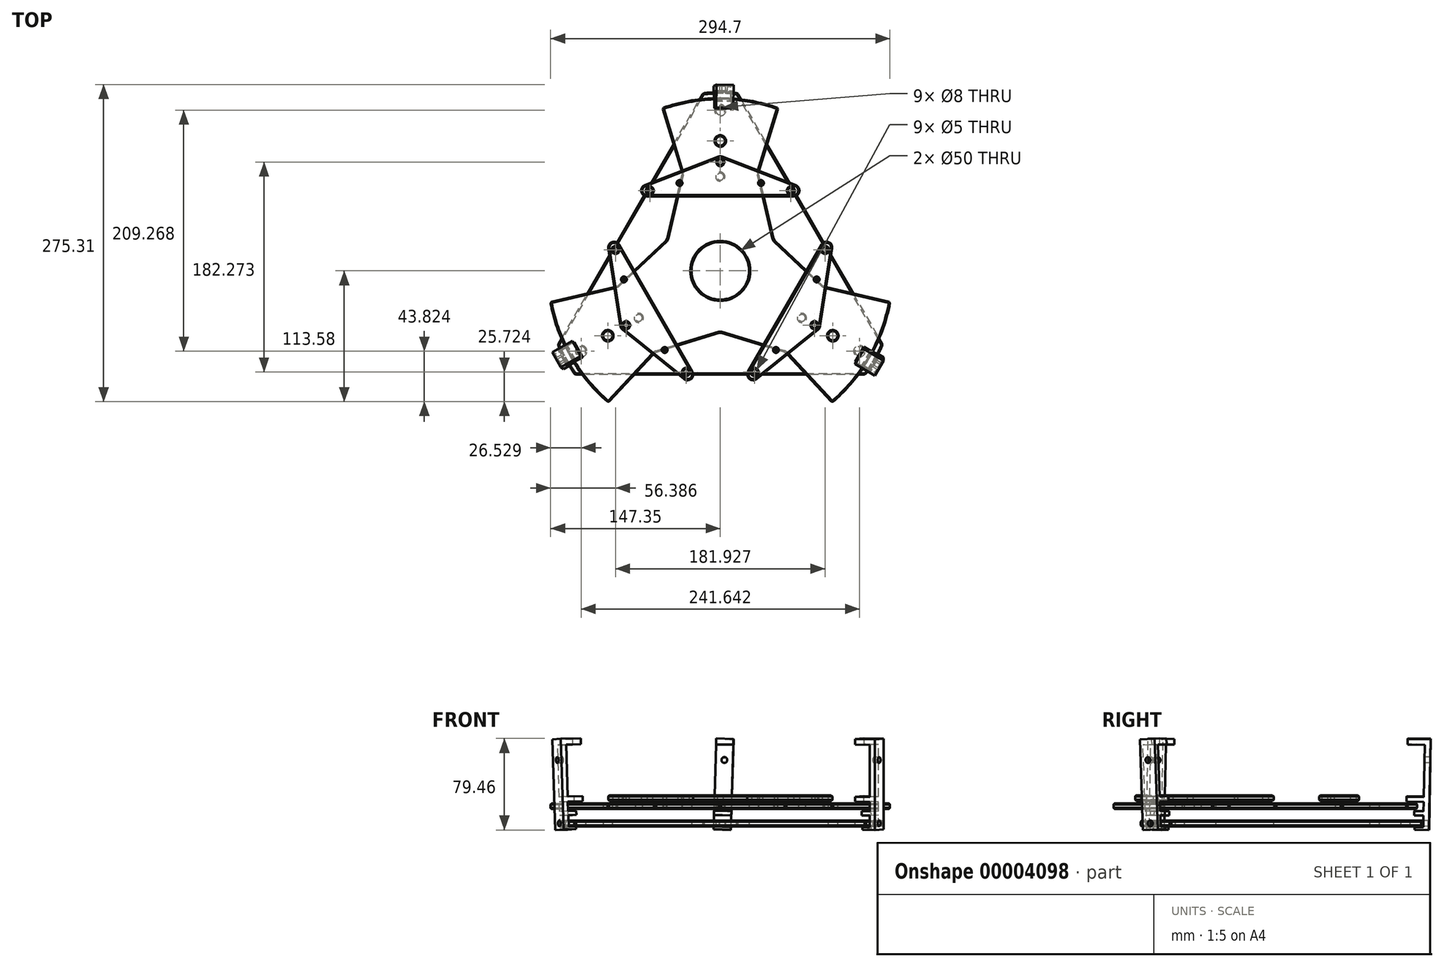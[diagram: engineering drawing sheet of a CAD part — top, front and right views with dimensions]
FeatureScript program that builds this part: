
annotation { "Feature Type Name" : "Feature", "Feature Type Description" : "" }
export const myFeature = defineFeature(function(context is Context, id is Id, definition is map)
    precondition{}
    {
        {
            var Q0;
            Q0=qCreatedBy(makeId("Top.planeOp"),FACE);
            var sketch = newSketch(context, id + "F0", { "sketchPlane" : qUnion([Q0])});
            skArc(sketch, "E0", {"start": v(-141.07, -64.21) * mm, "mid": v(-134.23, -77.5) * mm, "end": v(-126.15, -90.07) * mm});
            skCircle(sketch, "E1.cCircle", {"center": v(0, 0) * mm, "radius": 90.07 * mm, "construction": true});
            skLineSegment(sketch, "E1.0", {"start": v(14.93, 154.28) * mm, "end": v(141.07, -64.21) * mm});
            skLineSegment(sketch, "E1.1", {"start": v(126.15, -90.07) * mm, "end": v(-126.15, -90.07) * mm});
            skLineSegment(sketch, "E1.2", {"start": v(-141.07, -64.21) * mm, "end": v(-14.93, 154.28) * mm});
            skPoint(sketch, "E1.0.midPoint", {"position": v(78, 45.03) * mm});
            skPoint(sketch, "E2.orphan", {"position": v(0, 180.13) * mm});
            skPoint(sketch, "E3.orphan", {"position": v(-156, -90.07) * mm});
            skPoint(sketch, "E4.orphan", {"position": v(156, -90.07) * mm});
            skArc(sketch, "E5.trimOffspring", {"start": v(126.15, -90.07) * mm, "mid": v(134.23, -77.5) * mm, "end": v(141.07, -64.21) * mm});
            skArc(sketch, "E6.trimOffspring", {"start": v(14.93, 154.28) * mm, "mid": v(0, 155) * mm, "end": v(-14.93, 154.28) * mm});
            skCircle(sketch, "E7", {"center": v(0, 0) * mm, "radius": 25 * mm});
            skCircle(sketch, "E8", {"center": v(0, 112.79) * mm, "radius": 4 * mm});
            skCircle(sketch, "E9.1.0", {"center": v(-97.68, -56.4) * mm, "radius": 4 * mm});
            skCircle(sketch, "E9.2.0", {"center": v(97.68, -56.4) * mm, "radius": 4 * mm});
            skCircle(sketch, "E10", {"center": v(0, 139.51) * mm, "radius": 4 * mm});
            skCircle(sketch, "E11.1.0", {"center": v(-120.82, -69.76) * mm, "radius": 4 * mm});
            skCircle(sketch, "E11.2.0", {"center": v(120.82, -69.76) * mm, "radius": 4 * mm});
            skSolve(sketch);
        }
        {
            var Q0;
            Q0=makeQuery(id+"F0.imprint","IMPRINT",FACE,{"disambiguationData":[TD([[makeQuery(id+"F0.imprint","IMPRINT",EDGE,{"derivedFrom":sQuery(id+"F0.wireOp",EDGE,"E0")}),1.0]])]});
            extrude(context, id + "F1", {"entities" : qUnion([Q0]), "depth" : 5 * mm});
        }
        {
            var Q0;
            Q0=makeQuery(id+"F1.opExtrude","CAP_FACE",FACE,{"disambiguationData":[OSD([sQuery(id+"F0.wireOp",EDGE,"E0"),sQuery(id+"F0.wireOp",EDGE,"E1.0"),sQuery(id+"F0.wireOp",EDGE,"E1.1"),sQuery(id+"F0.wireOp",EDGE,"E1.2"),sQuery(id+"F0.wireOp",EDGE,"E5.trimOffspring"),sQuery(id+"F0.wireOp",EDGE,"E6.trimOffspring"),sQuery(id+"F0.wireOp",EDGE,"E7"),sQuery(id+"F0.wireOp",EDGE,"E8"),sQuery(id+"F0.wireOp",EDGE,"E9.1.0"),sQuery(id+"F0.wireOp",EDGE,"E9.2.0"),sQuery(id+"F0.wireOp",EDGE,"E10"),sQuery(id+"F0.wireOp",EDGE,"E11.1.0"),sQuery(id+"F0.wireOp",EDGE,"E11.2.0")])],"isStart":false});
            cPlane(context, id + "F2", {"entities" : qUnion([Q0]), "cplaneType" : CPlaneType.OFFSET, "offset" : 10 * mm, "width" : 150 * mm, "height" : 150 * mm});
        }
        {
            var Q0;
            Q0=qCreatedBy(id+"F2.planeOp",FACE);
            var sketch = newSketch(context, id + "F3", { "sketchPlane" : qUnion([Q0])});
            skCircle(sketch, "E12.0", {"center": v(0, 0) * mm, "radius": 25 * mm});
            skArc(sketch, "E13.0", {"start": v(14.93, 154.28) * mm, "mid": v(0, 155) * mm, "end": v(-14.93, 154.28) * mm, "construction": true});
            skLineSegment(sketch, "E14", {"start": v(-50.32, 141.3) * mm, "end": v(-32.94, 84.6) * mm});
            skCircle(sketch, "E15", {"center": v(0, 0) * mm, "radius": 53.68 * mm, "construction": true});
            skLineSegment(sketch, "E16", {"start": v(-32.94, 84.6) * mm, "end": v(-46.49, 26.84) * mm});
            skCircle(sketch, "E17.cCircle", {"center": v(0, 0) * mm, "radius": 26.84 * mm, "construction": true});
            skLineSegment(sketch, "E17.0", {"start": v(-46.49, 26.84) * mm, "end": v(46.49, 26.84) * mm, "construction": true});
            skLineSegment(sketch, "E17.1", {"start": v(46.49, 26.84) * mm, "end": v(0, -53.68) * mm, "construction": true});
            skLineSegment(sketch, "E17.2", {"start": v(0, -53.68) * mm, "end": v(-46.49, 26.84) * mm, "construction": true});
            skPoint(sketch, "E17.0.midPoint", {"position": v(0, 26.84) * mm});
            skLineSegment(sketch, "E18.0.MirrorCS", {"start": v(32.94, 84.6) * mm, "end": v(46.49, 26.84) * mm});
            skLineSegment(sketch, "E18.1.MirrorCS", {"start": v(50.32, 141.3) * mm, "end": v(32.94, 84.6) * mm});
            skArc(sketch, "E19.0", {"start": v(-50.32, 141.3) * mm, "mid": v(0, 150) * mm, "end": v(50.32, 141.3) * mm});
            skLineSegment(sketch, "E20.1.0", {"start": v(-56.79, -70.82) * mm, "end": v(0, -53.68) * mm});
            skLineSegment(sketch, "E20.1.1", {"start": v(-97.22, -114.23) * mm, "end": v(-56.79, -70.82) * mm});
            skArc(sketch, "E20.1.2", {"start": v(-97.22, -114.23) * mm, "mid": v(-129.9, -75) * mm, "end": v(-147.54, -27.08) * mm});
            skLineSegment(sketch, "E20.1.3", {"start": v(-147.54, -27.08) * mm, "end": v(-89.73, -13.77) * mm});
            skLineSegment(sketch, "E20.1.4", {"start": v(-89.73, -13.77) * mm, "end": v(-46.49, 26.84) * mm});
            skLineSegment(sketch, "E20.2.0", {"start": v(89.73, -13.77) * mm, "end": v(46.49, 26.84) * mm});
            skLineSegment(sketch, "E20.2.1", {"start": v(147.54, -27.08) * mm, "end": v(89.73, -13.77) * mm});
            skArc(sketch, "E20.2.2", {"start": v(147.54, -27.08) * mm, "mid": v(129.9, -75) * mm, "end": v(97.22, -114.23) * mm});
            skLineSegment(sketch, "E20.2.3", {"start": v(97.22, -114.23) * mm, "end": v(56.79, -70.82) * mm});
            skLineSegment(sketch, "E20.2.4", {"start": v(56.79, -70.82) * mm, "end": v(0, -53.68) * mm});
            skCircle(sketch, "E21.0", {"center": v(-97.68, -56.4) * mm, "radius": 4 * mm});
            skCircle(sketch, "E22.0", {"center": v(0, 112.79) * mm, "radius": 4 * mm});
            skCircle(sketch, "E23.0", {"center": v(97.68, -56.4) * mm, "radius": 4 * mm});
            skCircle(sketch, "E24", {"center": v(0, 81.76) * mm, "radius": 3 * mm});
            skCircle(sketch, "E25.1.0", {"center": v(-70.8, -40.88) * mm, "radius": 3 * mm});
            skCircle(sketch, "E25.2.0", {"center": v(70.8, -40.88) * mm, "radius": 3 * mm});
            skSolve(sketch);
        }
        {
            var Q0;
            Q0=makeQuery(id+"F3.imprint","IMPRINT",FACE,{"disambiguationData":[TD([[makeQuery(id+"F3.imprint","IMPRINT",EDGE,{"derivedFrom":sQuery(id+"F3.wireOp",EDGE,"E12.0")}),-1.0]])]});
            extrude(context, id + "F4", {"entities" : qUnion([Q0]), "depth" : 5 * mm});
        }
        {
            var Q0;
            Q0=makeQuery(id+"F4.opExtrude","CAP_FACE",FACE,{"disambiguationData":[OSD([sQuery(id+"F3.wireOp",EDGE,"E12.0"),sQuery(id+"F3.wireOp",EDGE,"E14"),sQuery(id+"F3.wireOp",EDGE,"E16"),sQuery(id+"F3.wireOp",EDGE,"E18.0.MirrorCS"),sQuery(id+"F3.wireOp",EDGE,"E18.1.MirrorCS"),sQuery(id+"F3.wireOp",EDGE,"E19.0"),sQuery(id+"F3.wireOp",EDGE,"E20.1.0"),sQuery(id+"F3.wireOp",EDGE,"E20.1.1"),sQuery(id+"F3.wireOp",EDGE,"E20.1.2"),sQuery(id+"F3.wireOp",EDGE,"E20.1.3"),sQuery(id+"F3.wireOp",EDGE,"E20.1.4"),sQuery(id+"F3.wireOp",EDGE,"E20.2.0"),sQuery(id+"F3.wireOp",EDGE,"E20.2.1"),sQuery(id+"F3.wireOp",EDGE,"E20.2.2"),sQuery(id+"F3.wireOp",EDGE,"E20.2.3"),sQuery(id+"F3.wireOp",EDGE,"E20.2.4"),sQuery(id+"F3.wireOp",EDGE,"E21.0"),sQuery(id+"F3.wireOp",EDGE,"E22.0"),sQuery(id+"F3.wireOp",EDGE,"E23.0"),sQuery(id+"F3.wireOp",EDGE,"E24"),sQuery(id+"F3.wireOp",EDGE,"E25.1.0"),sQuery(id+"F3.wireOp",EDGE,"E25.2.0")])],"isStart":false});
            cPlane(context, id + "F5", {"entities" : qUnion([Q0]), "cplaneType" : CPlaneType.OFFSET, "offset" : 2 * mm, "width" : 150 * mm, "height" : 150 * mm});
        }
        {
            var Q0;
            Q0=qCreatedBy(id+"F5.planeOp",FACE);
            var sketch = newSketch(context, id + "F6", { "sketchPlane" : qUnion([Q0])});
            skCircle(sketch, "E26", {"center": v(0, 0) * mm, "radius": 94.42 * mm, "construction": true});
            skLineSegment(sketch, "E27", {"start": v(-63.7, 69.7) * mm, "end": v(63.7, 69.7) * mm, "construction": true});
            skLineSegment(sketch, "E28", {"start": v(63.7, 69.7) * mm, "end": v(0, 94.42) * mm, "construction": true});
            skLineSegment(sketch, "E29", {"start": v(0, 94.42) * mm, "end": v(-63.7, 69.7) * mm, "construction": true});
            skLineSegment(sketch, "E30.0", {"start": v(-1.8, 99.08) * mm, "end": v(-65.5, 74.36) * mm});
            skLineSegment(sketch, "E30.1", {"start": v(65.5, 74.36) * mm, "end": v(1.8, 99.08) * mm});
            skLineSegment(sketch, "E30.2", {"start": v(-63.7, 64.7) * mm, "end": v(63.7, 64.7) * mm});
            skLineSegment(sketch, "E31.0", {"start": v(0, 99.78) * mm, "end": v(-90.4, 64.7) * mm, "construction": true});
            skLineSegment(sketch, "E31.1", {"start": v(90.4, 64.7) * mm, "end": v(0, 99.78) * mm, "construction": true});
            skLineSegment(sketch, "E31.2", {"start": v(-90.4, 64.7) * mm, "end": v(90.4, 64.7) * mm, "construction": true});
            skPoint(sketch, "E32.visualSharp", {"position": v(-90.4, 64.7) * mm});
            skArc(sketch, "E32.filletArc", {"start": v(-65.5, 74.36) * mm, "mid": v(-68.6, 68.78) * mm, "end": v(-63.7, 64.7) * mm});
            skPoint(sketch, "E33.visualSharp", {"position": v(90.4, 64.7) * mm});
            skArc(sketch, "E33.filletArc", {"start": v(63.7, 64.7) * mm, "mid": v(68.6, 68.78) * mm, "end": v(65.5, 74.36) * mm});
            skPoint(sketch, "E34.visualSharp", {"position": v(0, 99.78) * mm});
            skArc(sketch, "E34.filletArc", {"start": v(1.8, 99.08) * mm, "mid": v(0, 99.42) * mm, "end": v(-1.8, 99.08) * mm});
            skCircle(sketch, "E35", {"center": v(-35.37, 76.2) * mm, "radius": 1.5 * mm});
            skCircle(sketch, "E36.0.MirrorC", {"center": v(35.37, 76.2) * mm, "radius": 1.5 * mm});
            skCircle(sketch, "E37", {"center": v(0, 94.42) * mm, "radius": 2.5 * mm});
            skCircle(sketch, "E38", {"center": v(-61.2, 69.7) * mm, "radius": 2.5 * mm});
            skCircle(sketch, "E39.0.MirrorC", {"center": v(61.2, 69.7) * mm, "radius": 2.5 * mm});
            skLineSegment(sketch, "E40.1.0", {"start": v(-28.51, -90) * mm, "end": v(-92.2, 20.31) * mm, "construction": true});
            skLineSegment(sketch, "E40.1.1", {"start": v(-84.9, -51.1) * mm, "end": v(-31.65, -93.9) * mm});
            skLineSegment(sketch, "E40.1.2", {"start": v(-81.77, -47.2) * mm, "end": v(-28.51, -90) * mm, "construction": true});
            skPoint(sketch, "E40.1.3", {"position": v(-10.83, -110.63) * mm});
            skLineSegment(sketch, "E40.1.4", {"start": v(-92.2, 20.31) * mm, "end": v(-81.77, -47.2) * mm, "construction": true});
            skArc(sketch, "E40.1.5", {"start": v(-87.88, 22.81) * mm, "mid": v(-93.87, 25.03) * mm, "end": v(-97.15, 19.55) * mm});
            skLineSegment(sketch, "E40.1.6", {"start": v(-97.15, 19.55) * mm, "end": v(-86.7, -47.97) * mm});
            skCircle(sketch, "E40.1.7", {"center": v(-81.77, -47.2) * mm, "radius": 2.5 * mm});
            skCircle(sketch, "E40.1.8", {"center": v(-83.67, -7.47) * mm, "radius": 1.5 * mm});
            skLineSegment(sketch, "E40.1.9", {"start": v(-86.41, -49.9) * mm, "end": v(-10.83, -110.63) * mm, "construction": true});
            skArc(sketch, "E40.1.10", {"start": v(-31.65, -93.9) * mm, "mid": v(-25.26, -93.8) * mm, "end": v(-24.18, -87.5) * mm});
            skCircle(sketch, "E40.1.11", {"center": v(-90.96, 18.16) * mm, "radius": 2.5 * mm});
            skLineSegment(sketch, "E40.1.12", {"start": v(-24.18, -87.5) * mm, "end": v(-87.88, 22.81) * mm});
            skPoint(sketch, "E40.1.13", {"position": v(-86.41, -49.9) * mm});
            skCircle(sketch, "E40.1.14", {"center": v(-48.3, -68.72) * mm, "radius": 1.5 * mm});
            skCircle(sketch, "E40.1.15", {"center": v(-29.76, -87.86) * mm, "radius": 2.5 * mm});
            skArc(sketch, "E40.1.16", {"start": v(-86.7, -47.97) * mm, "mid": v(-86.1, -49.7) * mm, "end": v(-84.9, -51.1) * mm});
            skLineSegment(sketch, "E40.2.0", {"start": v(92.2, 20.31) * mm, "end": v(28.51, -90) * mm, "construction": true});
            skLineSegment(sketch, "E40.2.1", {"start": v(86.7, -47.97) * mm, "end": v(97.15, 19.55) * mm});
            skLineSegment(sketch, "E40.2.2", {"start": v(81.77, -47.2) * mm, "end": v(92.2, 20.31) * mm, "construction": true});
            skPoint(sketch, "E40.2.3", {"position": v(101.23, 45.94) * mm});
            skLineSegment(sketch, "E40.2.4", {"start": v(28.51, -90) * mm, "end": v(81.77, -47.2) * mm, "construction": true});
            skArc(sketch, "E40.2.5", {"start": v(24.18, -87.5) * mm, "mid": v(25.26, -93.8) * mm, "end": v(31.65, -93.9) * mm});
            skLineSegment(sketch, "E40.2.6", {"start": v(31.65, -93.9) * mm, "end": v(84.9, -51.1) * mm});
            skCircle(sketch, "E40.2.7", {"center": v(81.77, -47.2) * mm, "radius": 2.5 * mm});
            skCircle(sketch, "E40.2.8", {"center": v(48.3, -68.72) * mm, "radius": 1.5 * mm});
            skLineSegment(sketch, "E40.2.9", {"start": v(86.41, -49.9) * mm, "end": v(101.23, 45.94) * mm, "construction": true});
            skArc(sketch, "E40.2.10", {"start": v(97.15, 19.55) * mm, "mid": v(93.87, 25.03) * mm, "end": v(87.88, 22.81) * mm});
            skCircle(sketch, "E40.2.11", {"center": v(29.76, -87.86) * mm, "radius": 2.5 * mm});
            skLineSegment(sketch, "E40.2.12", {"start": v(87.88, 22.81) * mm, "end": v(24.18, -87.5) * mm});
            skPoint(sketch, "E40.2.13", {"position": v(86.41, -49.9) * mm});
            skCircle(sketch, "E40.2.14", {"center": v(83.67, -7.47) * mm, "radius": 1.5 * mm});
            skCircle(sketch, "E40.2.15", {"center": v(90.96, 18.16) * mm, "radius": 2.5 * mm});
            skArc(sketch, "E40.2.16", {"start": v(84.9, -51.1) * mm, "mid": v(86.1, -49.7) * mm, "end": v(86.7, -47.97) * mm});
            skSolve(sketch);
        }
        {
            var Q0;
            {Q0=qUnion([makeQuery(id+"F6.imprint","IMPRINT",FACE,{"disambiguationData":[TD([[makeQuery(id+"F6.imprint","IMPRINT",EDGE,{"derivedFrom":sQuery(id+"F6.wireOp",EDGE,"E30.0")}),1.0]])]}),makeQuery(id+"F6.imprint","IMPRINT",FACE,{"disambiguationData":[TD([[makeQuery(id+"F6.imprint","IMPRINT",EDGE,{"derivedFrom":sQuery(id+"F6.wireOp",EDGE,"E40.1.1")}),1.0]])]}),makeQuery(id+"F6.imprint","IMPRINT",FACE,{"disambiguationData":[TD([[makeQuery(id+"F6.imprint","IMPRINT",EDGE,{"derivedFrom":sQuery(id+"F6.wireOp",EDGE,"E40.2.1")}),1.0]])]})]);}
            extrude(context, id + "F7", {"entities" : qUnion([Q0]), "depth" : 5 * mm});
        }
        {
            var Q0;
            Q0=qCreatedBy(makeId("Origin.pointOp"),VERTEX);
            var Q1;
            Q1=makeQuery(id+"F7.opExtrude","CAP_VERTEX",VERTEX,{"disambiguationData":[OSD([sQuery(id+"F6.wireOp",EDGE,"E40.2.6"),sQuery(id+"F6.wireOp",EDGE,"E40.2.16")])],"isStart":true});
            var Q2;
            Q2=makeQuery(id+"F4.opExtrude","CAP_VERTEX",VERTEX,{"disambiguationData":[OSD([sQuery(id+"F3.wireOp",EDGE,"E16"),sQuery(id+"F3.wireOp",EDGE,"E20.1.4")])],"isStart":false});
            cPlane(context, id + "F8", {"entities" : qUnion([Q0, Q1, Q2]), "cplaneType" : CPlaneType.THREE_POINT, "offset" : 150 * mm, "width" : 150 * mm, "height" : 150 * mm});
        }
        {
            var Q0;
            Q0=qCreatedBy(id+"F8.planeOp",FACE);
            var sketch = newSketch(context, id + "F9", { "sketchPlane" : qUnion([Q0])});
            skLineSegment(sketch, "E41.bottom", {"start": v(-155.27, 0) * mm, "end": v(-160.27, 0) * mm});
            skLineSegment(sketch, "E41.left", {"start": v(-155.27, 2.3) * mm, "end": v(-155.27, 12.37) * mm});
            skLineSegment(sketch, "E41.right", {"start": v(-160.27, 0) * mm, "end": v(-160.27, 73.75) * mm});
            skLineSegment(sketch, "E42.0", {"start": v(65.82, -0.5) * mm, "end": v(-154, 7.29) * mm, "construction": true});
            skLineSegment(sketch, "E43.right", {"start": v(-155.27, 20.95) * mm, "end": v(-155.27, 24.23) * mm});
            skPoint(sketch, "E44.0", {"position": v(-140.46, 15.96) * mm});
            skLineSegment(sketch, "E45.top", {"start": v(-147.28, 12.37) * mm, "end": v(-155.27, 12.37) * mm});
            skLineSegment(sketch, "E45.left", {"start": v(-147.24, 16.1) * mm, "end": v(-147.28, 12.37) * mm});
            skLineSegment(sketch, "E46.bottom", {"start": v(-155.27, 73.75) * mm, "end": v(-140.4, 73.75) * mm});
            skLineSegment(sketch, "E46.top", {"start": v(-155.27, 78.7) * mm, "end": v(-140.4, 78.7) * mm});
            skLineSegment(sketch, "E46.right", {"start": v(-140.4, 78.7) * mm, "end": v(-140.4, 73.75) * mm});
            skPoint(sketch, "E47.0", {"position": v(-154.08, 2.3) * mm});
            skLineSegment(sketch, "E48.bottom", {"start": v(-155.27, 0) * mm, "end": v(-147.91, 0) * mm});
            skLineSegment(sketch, "E48.top", {"start": v(-155.27, 2.3) * mm, "end": v(-147.91, 2.3) * mm});
            skLineSegment(sketch, "E48.right", {"start": v(-147.91, 0) * mm, "end": v(-147.91, 2.3) * mm});
            skLineSegment(sketch, "E49.top", {"start": v(-155.27, 78.7) * mm, "end": v(-160.27, 78.7) * mm});
            skLineSegment(sketch, "E49.right", {"start": v(-160.27, 73.75) * mm, "end": v(-160.27, 78.7) * mm});
            skLineSegment(sketch, "E50.bottom", {"start": v(-140.46, 24.23) * mm, "end": v(-155.27, 24.23) * mm});
            skLineSegment(sketch, "E50.top", {"start": v(-140.46, 28.52) * mm, "end": v(-155.27, 28.52) * mm});
            skLineSegment(sketch, "E50.left", {"start": v(-140.46, 24.23) * mm, "end": v(-140.46, 28.52) * mm});
            skLineSegment(sketch, "E51.trimOffspring", {"start": v(-155.27, 28.52) * mm, "end": v(-155.27, 73.75) * mm});
            skLineSegment(sketch, "E52.trimOffspring", {"start": v(-155.27, 15.96) * mm, "end": v(-155.27, 24.23) * mm});
            skLineSegment(sketch, "E53", {"start": v(-147.24, 16.1) * mm, "end": v(-155.27, 15.96) * mm});
            skSolve(sketch);
        }
        {
            var Q0;
            Q0 = qSketchRegion(id + "F9", true);
            extrude(context, id + "F10", {"entities" : qUnion([Q0]), "operationType" : NewBodyOperationType.ADD, "depth" : 15 * mm, "symmetric" : true});
        }
        {
            var Q0;
            Q0=makeQuery(id+"F10.opExtrude","SWEPT_BODY",BODY,{"disambiguationData":[OSD([sQuery(id+"F9.wireOp",EDGE,"E41.bottom"),sQuery(id+"F9.wireOp",EDGE,"E41.left"),sQuery(id+"F9.wireOp",EDGE,"E45.top"),sQuery(id+"F9.wireOp",EDGE,"E45.left"),sQuery(id+"F9.wireOp",EDGE,"E46.bottom"),sQuery(id+"F9.wireOp",EDGE,"E46.top"),sQuery(id+"F9.wireOp",EDGE,"E46.right"),sQuery(id+"F9.wireOp",EDGE,"E48.top"),sQuery(id+"F9.wireOp",EDGE,"E48.right"),sQuery(id+"F9.wireOp",EDGE,"E49.right"),sQuery(id+"F9.wireOp",EDGE,"E50.bottom"),sQuery(id+"F9.wireOp",EDGE,"E50.top"),sQuery(id+"F9.wireOp",EDGE,"E50.left"),sQuery(id+"F9.wireOp",EDGE,"E51.trimOffspring"),sQuery(id+"F9.wireOp",EDGE,"E52.trimOffspring"),sQuery(id+"F9.wireOp",EDGE,"E53")])]});
            var Q1;
            Q1=makeQuery(id+"F4.opExtrude","CAP_EDGE",EDGE,{"disambiguationData":[OSD([sQuery(id+"F3.wireOp",EDGE,"E12.0")])],"isStart":false});
            circularPattern(context, id + "F11", {"entities" : qUnion([Q0]), "axis" : qUnion([Q1]), "angle" : 120 * degree, "instanceCount" : 3, "computeTransformsWithoutBuiltin" : true});
        }
        {
            var Q0;
            Q0=makeQuery(id+"F10.opExtrude","SWEPT_EDGE",EDGE,{"disambiguationData":[OSD([sQuery(id+"F9.wireOp",EDGE,"E46.top"),sQuery(id+"F9.wireOp",EDGE,"E46.right")])]});
            var Q1;
            {var subQ0=sQuery(id+"F9.wireOp",EDGE,"E49.right");Q1=qUnion([makeQuery(id+"F10.opExtrude","SWEPT_EDGE",EDGE,{"disambiguationData":[OSD([sQuery(id+"F9.wireOp",EDGE,"E41.bottom"),subQ0])]}),makeQuery(id+"F10.opExtrude","SWEPT_EDGE",EDGE,{"disambiguationData":[OSD([sQuery(id+"F9.wireOp",EDGE,"E46.top"),subQ0])]})]);}
            var Q2;
            {var subQ0=sQuery(id+"F9.wireOp",EDGE,"E41.bottom");Q2=qUnion([makeQuery(id+"F10.opExtrude","SWEPT_EDGE",EDGE,{"disambiguationData":[OSD([subQ0,sQuery(id+"F9.wireOp",EDGE,"E49.right")])]}),makeQuery(id+"F10.opExtrude","SWEPT_EDGE",EDGE,{"disambiguationData":[OSD([subQ0,sQuery(id+"F9.wireOp",EDGE,"E48.right")])]})]);}
            var Q3;
            Q3=makeQuery(id+"F10.opExtrude","SWEPT_EDGE",EDGE,{"disambiguationData":[OSD([sQuery(id+"F9.wireOp",EDGE,"E50.top"),sQuery(id+"F9.wireOp",EDGE,"E50.left")])]});
            var Q4;
            {var subQ0=sQuery(id+"F9.wireOp",EDGE,"E49.right");Q4=qUnion([makeQuery(id+"F11.opPattern","COPY",EDGE,{"derivedFrom":makeQuery(id+"F10.opExtrude","SWEPT_EDGE",EDGE,{"disambiguationData":[OSD([sQuery(id+"F9.wireOp",EDGE,"E41.bottom"),subQ0])]}),"instanceName":"1"}),makeQuery(id+"F11.opPattern","COPY",EDGE,{"derivedFrom":makeQuery(id+"F10.opExtrude","SWEPT_EDGE",EDGE,{"disambiguationData":[OSD([sQuery(id+"F9.wireOp",EDGE,"E46.top"),subQ0])]}),"instanceName":"1"})]);}
            var Q5;
            Q5=makeQuery(id+"F11.opPattern","COPY",EDGE,{"derivedFrom":makeQuery(id+"F10.opExtrude","CAP_EDGE",EDGE,{"disambiguationData":[OSD([sQuery(id+"F9.wireOp",EDGE,"E41.left")])],"isStart":false}),"instanceName":"1"});
            var Q6;
            Q6=makeQuery(id+"F7.opExtrude","CAP_EDGE",EDGE,{"disambiguationData":[OSD([sQuery(id+"F6.wireOp",EDGE,"E40.1.1")])],"isStart":true});
            var Q7;
            Q7=makeQuery(id+"F11.opPattern","COPY",EDGE,{"derivedFrom":makeQuery(id+"F10.opExtrude","CAP_EDGE",EDGE,{"disambiguationData":[OSD([sQuery(id+"F9.wireOp",EDGE,"E41.left")])],"isStart":false}),"instanceName":"2"});
            var Q8;
            Q8=makeQuery(id+"F4.opExtrude","CAP_EDGE",EDGE,{"disambiguationData":[OSD([sQuery(id+"F3.wireOp",EDGE,"E23.0")])],"isStart":false});
            var Q9;
            Q9=makeQuery(id+"F11.opPattern","COPY",EDGE,{"derivedFrom":makeQuery(id+"F10.opExtrude","SWEPT_EDGE",EDGE,{"disambiguationData":[OSD([sQuery(id+"F9.wireOp",EDGE,"E50.top"),sQuery(id+"F9.wireOp",EDGE,"E50.left")])]}),"instanceName":"1"});
            var Q10;
            {var subQ0=sQuery(id+"F9.wireOp",EDGE,"E41.left");var subQ1=sQuery(id+"F9.wireOp",EDGE,"E50.top");Q10=qUnion([makeQuery(id+"F11.opPattern","COPY",EDGE,{"derivedFrom":makeQuery(id+"F10.opExtrude","SWEPT_EDGE",EDGE,{"disambiguationData":[OSD([subQ0,sQuery(id+"F9.wireOp",EDGE,"E48.top")])]}),"instanceName":"1"}),makeQuery(id+"F11.opPattern","COPY",EDGE,{"derivedFrom":makeQuery(id+"F10.opExtrude","SWEPT_EDGE",EDGE,{"disambiguationData":[OSD([subQ0,sQuery(id+"F9.wireOp",EDGE,"E45.top")])]}),"instanceName":"1"}),makeQuery(id+"F11.opPattern","COPY",EDGE,{"derivedFrom":makeQuery(id+"F10.opExtrude","SWEPT_EDGE",EDGE,{"disambiguationData":[OSD([subQ1,sQuery(id+"F9.wireOp",EDGE,"E50.left")])]}),"instanceName":"1"}),makeQuery(id+"F11.opPattern","COPY",EDGE,{"derivedFrom":makeQuery(id+"F10.opExtrude","SWEPT_EDGE",EDGE,{"disambiguationData":[OSD([subQ1,sQuery(id+"F9.wireOp",EDGE,"E51.trimOffspring")])]}),"instanceName":"1"})]);}
            var Q11;
            Q11=makeQuery(id+"F7.opExtrude","CAP_EDGE",EDGE,{"disambiguationData":[OSD([sQuery(id+"F6.wireOp",EDGE,"E40.1.1")])],"isStart":false});
            var Q12;
            Q12=makeQuery(id+"F7.opExtrude","CAP_EDGE",EDGE,{"disambiguationData":[OSD([sQuery(id+"F6.wireOp",EDGE,"E32.filletArc")])],"isStart":false});
            var Q13;
            Q13=makeQuery(id+"F11.opPattern","COPY",EDGE,{"derivedFrom":makeQuery(id+"F10.opExtrude","SWEPT_EDGE",EDGE,{"disambiguationData":[OSD([sQuery(id+"F9.wireOp",EDGE,"E50.bottom"),sQuery(id+"F9.wireOp",EDGE,"E50.left")])]}),"instanceName":"1"});
            var Q14;
            Q14=makeQuery(id+"F11.opPattern","COPY",EDGE,{"derivedFrom":makeQuery(id+"F10.opExtrude","SWEPT_EDGE",EDGE,{"disambiguationData":[OSD([sQuery(id+"F9.wireOp",EDGE,"E46.bottom"),sQuery(id+"F9.wireOp",EDGE,"E46.right")])]}),"instanceName":"1"});
            var Q15;
            Q15=makeQuery(id+"F11.opPattern","COPY",EDGE,{"derivedFrom":makeQuery(id+"F10.opExtrude","SWEPT_EDGE",EDGE,{"disambiguationData":[OSD([sQuery(id+"F9.wireOp",EDGE,"E46.top"),sQuery(id+"F9.wireOp",EDGE,"E46.right")])]}),"instanceName":"1"});
            var Q16;
            Q16=makeQuery(id+"F7.opExtrude","CAP_EDGE",EDGE,{"disambiguationData":[OSD([sQuery(id+"F6.wireOp",EDGE,"E30.2")])],"isStart":false});
            var Q17;
            Q17=makeQuery(id+"F7.opExtrude","CAP_EDGE",EDGE,{"disambiguationData":[OSD([sQuery(id+"F6.wireOp",EDGE,"E40.1.12")])],"isStart":false});
            var Q18;
            Q18=makeQuery(id+"F4.opExtrude","CAP_EDGE",EDGE,{"disambiguationData":[OSD([sQuery(id+"F3.wireOp",EDGE,"E20.2.1")])],"isStart":false});
            var Q19;
            Q19=makeQuery(id+"F4.opExtrude","CAP_EDGE",EDGE,{"disambiguationData":[OSD([sQuery(id+"F3.wireOp",EDGE,"E18.1.MirrorCS")])],"isStart":false});
            var Q20;
            Q20=makeQuery(id+"F11.opPattern","COPY",EDGE,{"derivedFrom":makeQuery(id+"F10.opExtrude","SWEPT_EDGE",EDGE,{"disambiguationData":[OSD([sQuery(id+"F9.wireOp",EDGE,"E46.top"),sQuery(id+"F9.wireOp",EDGE,"E46.right")])]}),"instanceName":"2"});
            var Q21;
            Q21=makeQuery(id+"F11.opPattern","COPY",EDGE,{"derivedFrom":makeQuery(id+"F10.opExtrude","CAP_EDGE",EDGE,{"disambiguationData":[OSD([sQuery(id+"F9.wireOp",EDGE,"E49.right")])],"isStart":false}),"instanceName":"2"});
            var Q22;
            Q22=makeQuery(id+"F4.opExtrude","CAP_EDGE",EDGE,{"disambiguationData":[OSD([sQuery(id+"F3.wireOp",EDGE,"E20.1.3")])],"isStart":false});
            var Q23;
            Q23=makeQuery(id+"F4.opExtrude","CAP_EDGE",EDGE,{"disambiguationData":[OSD([sQuery(id+"F3.wireOp",EDGE,"E14")])],"isStart":false});
            var Q24;
            Q24=makeQuery(id+"F4.opExtrude","CAP_EDGE",EDGE,{"disambiguationData":[OSD([sQuery(id+"F3.wireOp",EDGE,"E18.1.MirrorCS")])],"isStart":true});
            var Q25;
            Q25=makeQuery(id+"F10.opExtrude","CAP_EDGE",EDGE,{"disambiguationData":[OSD([sQuery(id+"F9.wireOp",EDGE,"E50.bottom")])],"isStart":true});
            var Q26;
            Q26=makeQuery(id+"F4.opExtrude","CAP_EDGE",EDGE,{"disambiguationData":[OSD([sQuery(id+"F3.wireOp",EDGE,"E19.0")])],"isStart":false});
            var Q27;
            Q27=makeQuery(id+"F4.opExtrude","CAP_EDGE",EDGE,{"disambiguationData":[OSD([sQuery(id+"F3.wireOp",EDGE,"E20.2.2")])],"isStart":false});
            var Q28;
            Q28=makeQuery(id+"F11.opPattern","COPY",EDGE,{"derivedFrom":makeQuery(id+"F10.opExtrude","CAP_EDGE",EDGE,{"disambiguationData":[OSD([sQuery(id+"F9.wireOp",EDGE,"E46.top")])],"isStart":false}),"instanceName":"1"});
            var Q29;
            Q29=makeQuery(id+"F11.opPattern","COPY",EDGE,{"derivedFrom":makeQuery(id+"F10.opExtrude","CAP_EDGE",EDGE,{"disambiguationData":[OSD([sQuery(id+"F9.wireOp",EDGE,"E46.top")])],"isStart":false}),"instanceName":"2"});
            var Q30;
            Q30=makeQuery(id+"F7.opExtrude","CAP_EDGE",EDGE,{"disambiguationData":[OSD([sQuery(id+"F6.wireOp",EDGE,"E40.1.6")])],"isStart":false});
            var Q31;
            Q31=makeQuery(id+"F7.opExtrude","CAP_EDGE",EDGE,{"disambiguationData":[OSD([sQuery(id+"F6.wireOp",EDGE,"E40.2.12")])],"isStart":false});
            var Q32;
            Q32=makeQuery(id+"F10.opExtrude","CAP_EDGE",EDGE,{"disambiguationData":[OSD([sQuery(id+"F9.wireOp",EDGE,"E46.bottom")])],"isStart":true});
            var Q33;
            Q33=makeQuery(id+"F10.opExtrude","CAP_EDGE",EDGE,{"disambiguationData":[OSD([sQuery(id+"F9.wireOp",EDGE,"E49.right")])],"isStart":false});
            var Q34;
            Q34=makeQuery(id+"F4.opExtrude","CAP_EDGE",EDGE,{"disambiguationData":[OSD([sQuery(id+"F3.wireOp",EDGE,"E20.2.2")])],"isStart":true});
            var Q35;
            Q35=makeQuery(id+"F4.opExtrude","CAP_EDGE",EDGE,{"disambiguationData":[OSD([sQuery(id+"F3.wireOp",EDGE,"E20.1.2")])],"isStart":false});
            var Q36;
            Q36=makeQuery(id+"F7.opExtrude","CAP_EDGE",EDGE,{"disambiguationData":[OSD([sQuery(id+"F6.wireOp",EDGE,"E40.2.1")])],"isStart":true});
            var Q37;
            Q37=makeQuery(id+"F10.opExtrude","CAP_EDGE",EDGE,{"disambiguationData":[OSD([sQuery(id+"F9.wireOp",EDGE,"E50.top")])],"isStart":true});
            var Q38;
            Q38=makeQuery(id+"F10.opExtrude","CAP_EDGE",EDGE,{"disambiguationData":[OSD([sQuery(id+"F9.wireOp",EDGE,"E45.top")])],"isStart":true});
            var Q39;
            Q39=makeQuery(id+"F4.opExtrude","CAP_EDGE",EDGE,{"disambiguationData":[OSD([sQuery(id+"F3.wireOp",EDGE,"E20.1.0")])],"isStart":false});
            var Q40;
            Q40=makeQuery(id+"F4.opExtrude","CAP_EDGE",EDGE,{"disambiguationData":[OSD([sQuery(id+"F3.wireOp",EDGE,"E20.2.3")])],"isStart":false});
            var Q41;
            Q41=makeQuery(id+"F7.opExtrude","CAP_EDGE",EDGE,{"disambiguationData":[OSD([sQuery(id+"F6.wireOp",EDGE,"E40.2.1")])],"isStart":false});
            var Q42;
            Q42=makeQuery(id+"F4.opExtrude","CAP_EDGE",EDGE,{"disambiguationData":[OSD([sQuery(id+"F3.wireOp",EDGE,"E20.2.3")])],"isStart":true});
            var Q43;
            Q43=makeQuery(id+"F4.opExtrude","CAP_EDGE",EDGE,{"disambiguationData":[OSD([sQuery(id+"F3.wireOp",EDGE,"E20.1.2")])],"isStart":true});
            var Q44;
            Q44=makeQuery(id+"F4.opExtrude","CAP_EDGE",EDGE,{"disambiguationData":[OSD([sQuery(id+"F3.wireOp",EDGE,"E20.2.4")])],"isStart":false});
            var Q45;
            Q45=makeQuery(id+"F4.opExtrude","CAP_EDGE",EDGE,{"disambiguationData":[OSD([sQuery(id+"F3.wireOp",EDGE,"E20.1.1")])],"isStart":false});
            var Q46;
            Q46=makeQuery(id+"F4.opExtrude","CAP_EDGE",EDGE,{"disambiguationData":[OSD([sQuery(id+"F3.wireOp",EDGE,"E20.2.4")])],"isStart":true});
            var Q47;
            Q47=makeQuery(id+"F11.opPattern","COPY",EDGE,{"derivedFrom":makeQuery(id+"F10.opExtrude","CAP_EDGE",EDGE,{"disambiguationData":[OSD([sQuery(id+"F9.wireOp",EDGE,"E46.top")])],"isStart":true}),"instanceName":"1"});
            var Q48;
            Q48=makeQuery(id+"F1.opExtrude","CAP_EDGE",EDGE,{"disambiguationData":[OSD([sQuery(id+"F0.wireOp",EDGE,"E1.0")])],"isStart":false});
            var Q49;
            Q49=makeQuery(id+"F1.opExtrude","CAP_EDGE",EDGE,{"disambiguationData":[OSD([sQuery(id+"F0.wireOp",EDGE,"E1.1")])],"isStart":true});
            var Q50;
            Q50=makeQuery(id+"F1.opExtrude","CAP_EDGE",EDGE,{"disambiguationData":[OSD([sQuery(id+"F0.wireOp",EDGE,"E1.1")])],"isStart":false});
            var Q51;
            Q51=makeQuery(id+"F1.opExtrude","CAP_EDGE",EDGE,{"disambiguationData":[OSD([sQuery(id+"F0.wireOp",EDGE,"E5.trimOffspring")])],"isStart":true});
            var Q52;
            Q52=makeQuery(id+"F1.opExtrude","CAP_EDGE",EDGE,{"disambiguationData":[OSD([sQuery(id+"F0.wireOp",EDGE,"E5.trimOffspring")])],"isStart":false});
            var Q53;
            Q53=makeQuery(id+"F11.opPattern","COPY",EDGE,{"derivedFrom":makeQuery(id+"F10.opExtrude","CAP_EDGE",EDGE,{"disambiguationData":[OSD([sQuery(id+"F9.wireOp",EDGE,"E46.bottom")])],"isStart":false}),"instanceName":"2"});
            var Q54;
            Q54=makeQuery(id+"F7.opExtrude","CAP_EDGE",EDGE,{"disambiguationData":[OSD([sQuery(id+"F6.wireOp",EDGE,"E40.2.6")])],"isStart":false});
            var Q55;
            Q55=makeQuery(id+"F7.opExtrude","CAP_EDGE",EDGE,{"disambiguationData":[OSD([sQuery(id+"F6.wireOp",EDGE,"E30.0")])],"isStart":false});
            var Q56;
            Q56=makeQuery(id+"F10.opExtrude","CAP_EDGE",EDGE,{"disambiguationData":[OSD([sQuery(id+"F9.wireOp",EDGE,"E46.top")])],"isStart":false});
            var Q57;
            Q57=makeQuery(id+"F11.opPattern","COPY",EDGE,{"derivedFrom":makeQuery(id+"F10.opExtrude","CAP_EDGE",EDGE,{"disambiguationData":[OSD([sQuery(id+"F9.wireOp",EDGE,"E50.top")])],"isStart":false}),"instanceName":"1"});
            var Q58;
            Q58=makeQuery(id+"F11.opPattern","COPY",EDGE,{"derivedFrom":makeQuery(id+"F10.opExtrude","CAP_EDGE",EDGE,{"disambiguationData":[OSD([sQuery(id+"F9.wireOp",EDGE,"E45.top")])],"isStart":false}),"instanceName":"2"});
            var Q59;
            Q59=makeQuery(id+"F11.opPattern","COPY",EDGE,{"derivedFrom":makeQuery(id+"F10.opExtrude","CAP_EDGE",EDGE,{"disambiguationData":[OSD([sQuery(id+"F9.wireOp",EDGE,"E50.top")])],"isStart":false}),"instanceName":"2"});
            var Q60;
            Q60=makeQuery(id+"F7.opExtrude","CAP_EDGE",EDGE,{"disambiguationData":[OSD([sQuery(id+"F6.wireOp",EDGE,"E30.1")])],"isStart":false});
            var Q61;
            Q61=makeQuery(id+"F11.opPattern","COPY",EDGE,{"derivedFrom":makeQuery(id+"F10.opExtrude","CAP_EDGE",EDGE,{"disambiguationData":[OSD([sQuery(id+"F9.wireOp",EDGE,"E45.bottom")])],"isStart":false}),"instanceName":"2"});
            var Q62;
            Q62=makeQuery(id+"F11.opPattern","COPY",EDGE,{"derivedFrom":makeQuery(id+"F10.opExtrude","CAP_EDGE",EDGE,{"disambiguationData":[OSD([sQuery(id+"F9.wireOp",EDGE,"E50.bottom")])],"isStart":false}),"instanceName":"2"});
            var Q63;
            {var subQ0=sQuery(id+"F9.wireOp",EDGE,"E49.right");Q63=qUnion([makeQuery(id+"F11.opPattern","COPY",EDGE,{"derivedFrom":makeQuery(id+"F10.opExtrude","SWEPT_EDGE",EDGE,{"disambiguationData":[OSD([sQuery(id+"F9.wireOp",EDGE,"E41.bottom"),subQ0])]}),"instanceName":"2"}),makeQuery(id+"F11.opPattern","COPY",EDGE,{"derivedFrom":makeQuery(id+"F10.opExtrude","SWEPT_EDGE",EDGE,{"disambiguationData":[OSD([sQuery(id+"F9.wireOp",EDGE,"E46.top"),subQ0])]}),"instanceName":"2"})]);}
            var Q64;
            Q64=makeQuery(id+"F11.opPattern","COPY",EDGE,{"derivedFrom":makeQuery(id+"F10.opExtrude","CAP_EDGE",EDGE,{"disambiguationData":[OSD([sQuery(id+"F9.wireOp",EDGE,"E50.top")])],"isStart":true}),"instanceName":"1"});
            var Q65;
            Q65=makeQuery(id+"F7.opExtrude","CAP_EDGE",EDGE,{"disambiguationData":[OSD([sQuery(id+"F6.wireOp",EDGE,"E30.2")])],"isStart":true});
            var Q66;
            Q66=makeQuery(id+"F11.opPattern","COPY",EDGE,{"derivedFrom":makeQuery(id+"F10.opExtrude","SWEPT_EDGE",EDGE,{"disambiguationData":[OSD([sQuery(id+"F9.wireOp",EDGE,"E50.top"),sQuery(id+"F9.wireOp",EDGE,"E50.left")])]}),"instanceName":"2"});
            var Q67;
            Q67=makeQuery(id+"F10.opExtrude","SWEPT_EDGE",EDGE,{"disambiguationData":[OSD([sQuery(id+"F9.wireOp",EDGE,"E45.top"),sQuery(id+"F9.wireOp",EDGE,"E45.left")])]});
            var Q68;
            Q68=makeQuery(id+"F10.opExtrude","SWEPT_EDGE",EDGE,{"disambiguationData":[OSD([sQuery(id+"F9.wireOp",EDGE,"E46.bottom"),sQuery(id+"F9.wireOp",EDGE,"E46.right")])]});
            var Q69;
            Q69=makeQuery(id+"F10.opExtrude","SWEPT_EDGE",EDGE,{"disambiguationData":[OSD([sQuery(id+"F9.wireOp",EDGE,"E41.left"),sQuery(id+"F9.wireOp",EDGE,"E45.top")])]});
            var Q70;
            {var subQ0=sQuery(id+"F9.wireOp",EDGE,"E41.left");var subQ1=sQuery(id+"F9.wireOp",EDGE,"E50.bottom");Q70=qUnion([makeQuery(id+"F10.opExtrude","SWEPT_EDGE",EDGE,{"disambiguationData":[OSD([subQ0,sQuery(id+"F9.wireOp",EDGE,"E48.top")])]}),makeQuery(id+"F10.opExtrude","SWEPT_EDGE",EDGE,{"disambiguationData":[OSD([subQ0,sQuery(id+"F9.wireOp",EDGE,"E45.top")])]}),makeQuery(id+"F10.opExtrude","SWEPT_EDGE",EDGE,{"disambiguationData":[OSD([subQ1,sQuery(id+"F9.wireOp",EDGE,"E50.left")])]}),makeQuery(id+"F10.opExtrude","SWEPT_EDGE",EDGE,{"disambiguationData":[OSD([subQ1,sQuery(id+"F9.wireOp",EDGE,"E52.trimOffspring")])]})]);}
            var Q71;
            {var subQ0=sQuery(id+"F9.wireOp",EDGE,"E41.left");var subQ1=sQuery(id+"F9.wireOp",EDGE,"E46.bottom");Q71=qUnion([makeQuery(id+"F10.opExtrude","SWEPT_EDGE",EDGE,{"disambiguationData":[OSD([subQ0,sQuery(id+"F9.wireOp",EDGE,"E48.top")])]}),makeQuery(id+"F10.opExtrude","SWEPT_EDGE",EDGE,{"disambiguationData":[OSD([subQ0,sQuery(id+"F9.wireOp",EDGE,"E45.top")])]}),makeQuery(id+"F10.opExtrude","SWEPT_EDGE",EDGE,{"disambiguationData":[OSD([subQ1,sQuery(id+"F9.wireOp",EDGE,"E51.trimOffspring")])]}),makeQuery(id+"F10.opExtrude","SWEPT_EDGE",EDGE,{"disambiguationData":[OSD([subQ1,sQuery(id+"F9.wireOp",EDGE,"E46.right")])]})]);}
            var Q72;
            {var subQ0=sQuery(id+"F9.wireOp",EDGE,"E41.left");Q72=qUnion([makeQuery(id+"F10.opExtrude","SWEPT_EDGE",EDGE,{"disambiguationData":[OSD([subQ0,sQuery(id+"F9.wireOp",EDGE,"E48.top")])]}),makeQuery(id+"F10.opExtrude","SWEPT_EDGE",EDGE,{"disambiguationData":[OSD([subQ0,sQuery(id+"F9.wireOp",EDGE,"E45.top")])]})]);}
            var Q73;
            {var subQ0=sQuery(id+"F9.wireOp",EDGE,"E45.left");Q73=qUnion([makeQuery(id+"F10.opExtrude","SWEPT_EDGE",EDGE,{"disambiguationData":[OSD([sQuery(id+"F9.wireOp",EDGE,"E45.top"),subQ0])]}),makeQuery(id+"F10.opExtrude","SWEPT_EDGE",EDGE,{"disambiguationData":[OSD([subQ0,sQuery(id+"F9.wireOp",EDGE,"E53")])]})]);}
            var Q74;
            Q74=makeQuery(id+"F10.opExtrude","SWEPT_EDGE",EDGE,{"disambiguationData":[OSD([sQuery(id+"F9.wireOp",EDGE,"E48.top"),sQuery(id+"F9.wireOp",EDGE,"E48.right")])]});
            var Q75;
            Q75=makeQuery(id+"F7.opExtrude","CAP_EDGE",EDGE,{"disambiguationData":[OSD([sQuery(id+"F6.wireOp",EDGE,"E40.1.5")])],"isStart":true});
            var Q76;
            Q76=makeQuery(id+"F7.opExtrude","CAP_EDGE",EDGE,{"disambiguationData":[OSD([sQuery(id+"F6.wireOp",EDGE,"E40.1.15")])],"isStart":true});
            var Q77;
            Q77=makeQuery(id+"F7.opExtrude","CAP_EDGE",EDGE,{"disambiguationData":[OSD([sQuery(id+"F6.wireOp",EDGE,"E40.2.11")])],"isStart":true});
            var Q78;
            Q78=makeQuery(id+"F4.opExtrude","CAP_EDGE",EDGE,{"disambiguationData":[OSD([sQuery(id+"F3.wireOp",EDGE,"E18.0.MirrorCS")])],"isStart":true});
            var Q79;
            Q79=makeQuery(id+"F4.opExtrude","CAP_EDGE",EDGE,{"disambiguationData":[OSD([sQuery(id+"F3.wireOp",EDGE,"E24")])],"isStart":true});
            var Q80;
            Q80=makeQuery(id+"F7.opExtrude","CAP_EDGE",EDGE,{"disambiguationData":[OSD([sQuery(id+"F6.wireOp",EDGE,"E33.filletArc")])],"isStart":true});
            var Q81;
            Q81=makeQuery(id+"F4.opExtrude","CAP_EDGE",EDGE,{"disambiguationData":[OSD([sQuery(id+"F3.wireOp",EDGE,"E20.2.0")])],"isStart":true});
            var Q82;
            Q82=makeQuery(id+"F10.opExtrude","SWEPT_EDGE",EDGE,{"disambiguationData":[OSD([sQuery(id+"F9.wireOp",EDGE,"E41.left"),sQuery(id+"F9.wireOp",EDGE,"E48.top")])]});
            var Q83;
            Q83=makeQuery(id+"F10.opExtrude","CAP_EDGE",EDGE,{"disambiguationData":[OSD([sQuery(id+"F9.wireOp",EDGE,"E50.top")])],"isStart":false});
            var Q84;
            Q84=makeQuery(id+"F10.opExtrude","CAP_EDGE",EDGE,{"disambiguationData":[OSD([sQuery(id+"F9.wireOp",EDGE,"E45.top")])],"isStart":false});
            var Q85;
            Q85=makeQuery(id+"F10.opExtrude","SWEPT_EDGE",EDGE,{"disambiguationData":[OSD([sQuery(id+"F9.wireOp",EDGE,"E50.bottom"),sQuery(id+"F9.wireOp",EDGE,"E50.left")])]});
            var Q86;
            {var subQ0=sQuery(id+"F9.wireOp",EDGE,"E41.left");var subQ1=sQuery(id+"F9.wireOp",EDGE,"E50.top");Q86=qUnion([makeQuery(id+"F10.opExtrude","SWEPT_EDGE",EDGE,{"disambiguationData":[OSD([subQ0,sQuery(id+"F9.wireOp",EDGE,"E48.top")])]}),makeQuery(id+"F10.opExtrude","SWEPT_EDGE",EDGE,{"disambiguationData":[OSD([subQ0,sQuery(id+"F9.wireOp",EDGE,"E45.top")])]}),makeQuery(id+"F10.opExtrude","SWEPT_EDGE",EDGE,{"disambiguationData":[OSD([subQ1,sQuery(id+"F9.wireOp",EDGE,"E50.left")])]}),makeQuery(id+"F10.opExtrude","SWEPT_EDGE",EDGE,{"disambiguationData":[OSD([subQ1,sQuery(id+"F9.wireOp",EDGE,"E51.trimOffspring")])]})]);}
            var Q87;
            Q87=makeQuery(id+"F1.opExtrude","CAP_EDGE",EDGE,{"disambiguationData":[OSD([sQuery(id+"F0.wireOp",EDGE,"E6.trimOffspring")])],"isStart":false});
            var Q88;
            {var subQ0=sQuery(id+"F9.wireOp",EDGE,"E48.right");Q88=qUnion([makeQuery(id+"F11.opPattern","COPY",EDGE,{"derivedFrom":makeQuery(id+"F10.opExtrude","SWEPT_EDGE",EDGE,{"disambiguationData":[OSD([sQuery(id+"F9.wireOp",EDGE,"E41.bottom"),subQ0])]}),"instanceName":"1"}),makeQuery(id+"F11.opPattern","COPY",EDGE,{"derivedFrom":makeQuery(id+"F10.opExtrude","SWEPT_EDGE",EDGE,{"disambiguationData":[OSD([sQuery(id+"F9.wireOp",EDGE,"E48.top"),subQ0])]}),"instanceName":"1"})]);}
            var Q89;
            Q89=makeQuery(id+"F7.opExtrude","CAP_EDGE",EDGE,{"disambiguationData":[OSD([sQuery(id+"F6.wireOp",EDGE,"E40.2.10")])],"isStart":true});
            var Q90;
            Q90=makeQuery(id+"F7.opExtrude","CAP_EDGE",EDGE,{"disambiguationData":[OSD([sQuery(id+"F6.wireOp",EDGE,"E40.1.14")])],"isStart":true});
            var Q91;
            Q91=makeQuery(id+"F11.opPattern","COPY",EDGE,{"derivedFrom":makeQuery(id+"F10.opExtrude","CAP_EDGE",EDGE,{"disambiguationData":[OSD([sQuery(id+"F9.wireOp",EDGE,"E48.top")])],"isStart":false}),"instanceName":"2"});
            var Q92;
            Q92=makeQuery(id+"F11.opPattern","COPY",EDGE,{"derivedFrom":makeQuery(id+"F10.opExtrude","SWEPT_EDGE",EDGE,{"disambiguationData":[OSD([sQuery(id+"F9.wireOp",EDGE,"E41.left"),sQuery(id+"F9.wireOp",EDGE,"E45.top")])]}),"instanceName":"2"});
            var Q93;
            {var subQ0=sQuery(id+"F9.wireOp",EDGE,"E41.left");var subQ1=sQuery(id+"F9.wireOp",EDGE,"E46.bottom");Q93=qUnion([makeQuery(id+"F11.opPattern","COPY",EDGE,{"derivedFrom":makeQuery(id+"F10.opExtrude","SWEPT_EDGE",EDGE,{"disambiguationData":[OSD([subQ0,sQuery(id+"F9.wireOp",EDGE,"E48.top")])]}),"instanceName":"1"}),makeQuery(id+"F11.opPattern","COPY",EDGE,{"derivedFrom":makeQuery(id+"F10.opExtrude","SWEPT_EDGE",EDGE,{"disambiguationData":[OSD([subQ0,sQuery(id+"F9.wireOp",EDGE,"E45.top")])]}),"instanceName":"1"}),makeQuery(id+"F11.opPattern","COPY",EDGE,{"derivedFrom":makeQuery(id+"F10.opExtrude","SWEPT_EDGE",EDGE,{"disambiguationData":[OSD([subQ1,sQuery(id+"F9.wireOp",EDGE,"E51.trimOffspring")])]}),"instanceName":"1"}),makeQuery(id+"F11.opPattern","COPY",EDGE,{"derivedFrom":makeQuery(id+"F10.opExtrude","SWEPT_EDGE",EDGE,{"disambiguationData":[OSD([subQ1,sQuery(id+"F9.wireOp",EDGE,"E46.right")])]}),"instanceName":"1"})]);}
            var Q94;
            Q94=makeQuery(id+"F4.opExtrude","CAP_EDGE",EDGE,{"disambiguationData":[OSD([sQuery(id+"F3.wireOp",EDGE,"E16")])],"isStart":false});
            var Q95;
            Q95=makeQuery(id+"F4.opExtrude","CAP_EDGE",EDGE,{"disambiguationData":[OSD([sQuery(id+"F3.wireOp",EDGE,"E20.1.4")])],"isStart":false});
            var Q96;
            Q96=makeQuery(id+"F7.opExtrude","CAP_EDGE",EDGE,{"disambiguationData":[OSD([sQuery(id+"F6.wireOp",EDGE,"E40.1.14")])],"isStart":false});
            var Q97;
            Q97=makeQuery(id+"F7.opExtrude","CAP_EDGE",EDGE,{"disambiguationData":[OSD([sQuery(id+"F6.wireOp",EDGE,"E40.2.10")])],"isStart":false});
            var Q98;
            Q98=makeQuery(id+"F4.opExtrude","CAP_EDGE",EDGE,{"disambiguationData":[OSD([sQuery(id+"F3.wireOp",EDGE,"E18.0.MirrorCS")])],"isStart":false});
            var Q99;
            Q99=makeQuery(id+"F4.opExtrude","CAP_EDGE",EDGE,{"disambiguationData":[OSD([sQuery(id+"F3.wireOp",EDGE,"E20.2.0")])],"isStart":false});
            var Q100;
            {var subQ0=sQuery(id+"F9.wireOp",EDGE,"E41.left");Q100=qUnion([makeQuery(id+"F11.opPattern","COPY",EDGE,{"derivedFrom":makeQuery(id+"F10.opExtrude","SWEPT_EDGE",EDGE,{"disambiguationData":[OSD([subQ0,sQuery(id+"F9.wireOp",EDGE,"E48.top")])]}),"instanceName":"1"}),makeQuery(id+"F11.opPattern","COPY",EDGE,{"derivedFrom":makeQuery(id+"F10.opExtrude","SWEPT_EDGE",EDGE,{"disambiguationData":[OSD([subQ0,sQuery(id+"F9.wireOp",EDGE,"E45.top")])]}),"instanceName":"1"})]);}
            var Q101;
            Q101=makeQuery(id+"F11.opPattern","COPY",EDGE,{"derivedFrom":makeQuery(id+"F10.opExtrude","SWEPT_EDGE",EDGE,{"disambiguationData":[OSD([sQuery(id+"F9.wireOp",EDGE,"E45.top"),sQuery(id+"F9.wireOp",EDGE,"E45.left")])]}),"instanceName":"1"});
            var Q102;
            {var subQ0=sQuery(id+"F9.wireOp",EDGE,"E41.left");var subQ1=sQuery(id+"F9.wireOp",EDGE,"E50.bottom");Q102=qUnion([makeQuery(id+"F11.opPattern","COPY",EDGE,{"derivedFrom":makeQuery(id+"F10.opExtrude","SWEPT_EDGE",EDGE,{"disambiguationData":[OSD([subQ0,sQuery(id+"F9.wireOp",EDGE,"E48.top")])]}),"instanceName":"1"}),makeQuery(id+"F11.opPattern","COPY",EDGE,{"derivedFrom":makeQuery(id+"F10.opExtrude","SWEPT_EDGE",EDGE,{"disambiguationData":[OSD([subQ0,sQuery(id+"F9.wireOp",EDGE,"E45.top")])]}),"instanceName":"1"}),makeQuery(id+"F11.opPattern","COPY",EDGE,{"derivedFrom":makeQuery(id+"F10.opExtrude","SWEPT_EDGE",EDGE,{"disambiguationData":[OSD([subQ1,sQuery(id+"F9.wireOp",EDGE,"E50.left")])]}),"instanceName":"1"}),makeQuery(id+"F11.opPattern","COPY",EDGE,{"derivedFrom":makeQuery(id+"F10.opExtrude","SWEPT_EDGE",EDGE,{"disambiguationData":[OSD([subQ1,sQuery(id+"F9.wireOp",EDGE,"E52.trimOffspring")])]}),"instanceName":"1"})]);}
            var Q103;
            {var subQ0=sQuery(id+"F9.wireOp",EDGE,"E45.left");Q103=qUnion([makeQuery(id+"F11.opPattern","COPY",EDGE,{"derivedFrom":makeQuery(id+"F10.opExtrude","SWEPT_EDGE",EDGE,{"disambiguationData":[OSD([sQuery(id+"F9.wireOp",EDGE,"E45.top"),subQ0])]}),"instanceName":"1"}),makeQuery(id+"F11.opPattern","COPY",EDGE,{"derivedFrom":makeQuery(id+"F10.opExtrude","SWEPT_EDGE",EDGE,{"disambiguationData":[OSD([subQ0,sQuery(id+"F9.wireOp",EDGE,"E53")])]}),"instanceName":"1"})]);}
            var Q104;
            Q104=makeQuery(id+"F4.opExtrude","CAP_EDGE",EDGE,{"disambiguationData":[OSD([sQuery(id+"F3.wireOp",EDGE,"E20.2.1")])],"isStart":true});
            var Q105;
            Q105=makeQuery(id+"F11.opPattern","COPY",EDGE,{"derivedFrom":makeQuery(id+"F10.opExtrude","CAP_EDGE",EDGE,{"disambiguationData":[OSD([sQuery(id+"F9.wireOp",EDGE,"E49.right")])],"isStart":true}),"instanceName":"1"});
            var Q106;
            Q106=makeQuery(id+"F11.opPattern","COPY",EDGE,{"derivedFrom":makeQuery(id+"F10.opExtrude","SWEPT_EDGE",EDGE,{"disambiguationData":[OSD([sQuery(id+"F9.wireOp",EDGE,"E46.bottom"),sQuery(id+"F9.wireOp",EDGE,"E46.right")])]}),"instanceName":"2"});
            var Q107;
            Q107=makeQuery(id+"F7.opExtrude","CAP_EDGE",EDGE,{"disambiguationData":[OSD([sQuery(id+"F6.wireOp",EDGE,"E39.0.MirrorC")])],"isStart":false});
            var Q108;
            Q108=makeQuery(id+"F7.opExtrude","CAP_EDGE",EDGE,{"disambiguationData":[OSD([sQuery(id+"F6.wireOp",EDGE,"E40.2.8")])],"isStart":false});
            var Q109;
            Q109=makeQuery(id+"F7.opExtrude","CAP_EDGE",EDGE,{"disambiguationData":[OSD([sQuery(id+"F6.wireOp",EDGE,"E32.filletArc")])],"isStart":true});
            var Q110;
            Q110=makeQuery(id+"F4.opExtrude","CAP_EDGE",EDGE,{"disambiguationData":[OSD([sQuery(id+"F3.wireOp",EDGE,"E23.0")])],"isStart":true});
            var Q111;
            Q111=makeQuery(id+"F4.opExtrude","CAP_EDGE",EDGE,{"disambiguationData":[OSD([sQuery(id+"F3.wireOp",EDGE,"E16")])],"isStart":true});
            var Q112;
            Q112=makeQuery(id+"F1.opExtrude","CAP_EDGE",EDGE,{"disambiguationData":[OSD([sQuery(id+"F0.wireOp",EDGE,"E7")])],"isStart":false});
            var Q113;
            Q113=makeQuery(id+"F4.opExtrude","CAP_EDGE",EDGE,{"disambiguationData":[OSD([sQuery(id+"F3.wireOp",EDGE,"E25.1.0")])],"isStart":false});
            var Q114;
            Q114=makeQuery(id+"F11.opPattern","COPY",EDGE,{"derivedFrom":makeQuery(id+"F10.opExtrude","CAP_EDGE",EDGE,{"disambiguationData":[OSD([sQuery(id+"F9.wireOp",EDGE,"E49.right")])],"isStart":false}),"instanceName":"1"});
            var Q115;
            Q115=makeQuery(id+"F4.opExtrude","CAP_EDGE",EDGE,{"disambiguationData":[OSD([sQuery(id+"F3.wireOp",EDGE,"E22.0")])],"isStart":false});
            var Q116;
            Q116=makeQuery(id+"F1.opExtrude","CAP_EDGE",EDGE,{"disambiguationData":[OSD([sQuery(id+"F0.wireOp",EDGE,"E7")])],"isStart":true});
            var Q117;
            Q117=makeQuery(id+"F10.opExtrude","CAP_EDGE",EDGE,{"disambiguationData":[OSD([sQuery(id+"F9.wireOp",EDGE,"E45.bottom")])],"isStart":true});
            var Q118;
            Q118=makeQuery(id+"F1.opExtrude","CAP_EDGE",EDGE,{"disambiguationData":[OSD([sQuery(id+"F0.wireOp",EDGE,"E11.2.0")])],"isStart":true});
            var Q119;
            Q119=makeQuery(id+"F11.opPattern","COPY",EDGE,{"derivedFrom":makeQuery(id+"F10.opExtrude","CAP_EDGE",EDGE,{"disambiguationData":[OSD([sQuery(id+"F9.wireOp",EDGE,"E41.left")])],"isStart":false}),"instanceName":"2"});
            var Q120;
            {var subQ0=sQuery(id+"F9.wireOp",EDGE,"E41.left");var subQ1=sQuery(id+"F9.wireOp",EDGE,"E50.bottom");Q120=qUnion([makeQuery(id+"F11.opPattern","COPY",EDGE,{"derivedFrom":makeQuery(id+"F10.opExtrude","SWEPT_EDGE",EDGE,{"disambiguationData":[OSD([subQ0,sQuery(id+"F9.wireOp",EDGE,"E48.top")])]}),"instanceName":"2"}),makeQuery(id+"F11.opPattern","COPY",EDGE,{"derivedFrom":makeQuery(id+"F10.opExtrude","SWEPT_EDGE",EDGE,{"disambiguationData":[OSD([subQ0,sQuery(id+"F9.wireOp",EDGE,"E45.top")])]}),"instanceName":"2"}),makeQuery(id+"F11.opPattern","COPY",EDGE,{"derivedFrom":makeQuery(id+"F10.opExtrude","SWEPT_EDGE",EDGE,{"disambiguationData":[OSD([subQ1,sQuery(id+"F9.wireOp",EDGE,"E50.left")])]}),"instanceName":"2"}),makeQuery(id+"F11.opPattern","COPY",EDGE,{"derivedFrom":makeQuery(id+"F10.opExtrude","SWEPT_EDGE",EDGE,{"disambiguationData":[OSD([subQ1,sQuery(id+"F9.wireOp",EDGE,"E52.trimOffspring")])]}),"instanceName":"2"})]);}
            var Q121;
            Q121=makeQuery(id+"F4.opExtrude","CAP_EDGE",EDGE,{"disambiguationData":[OSD([sQuery(id+"F3.wireOp",EDGE,"E14")])],"isStart":true});
            var Q122;
            Q122=makeQuery(id+"F4.opExtrude","CAP_EDGE",EDGE,{"disambiguationData":[OSD([sQuery(id+"F3.wireOp",EDGE,"E20.1.3")])],"isStart":true});
            var Q123;
            Q123=makeQuery(id+"F4.opExtrude","CAP_EDGE",EDGE,{"disambiguationData":[OSD([sQuery(id+"F3.wireOp",EDGE,"E22.0")])],"isStart":true});
            var Q124;
            Q124=makeQuery(id+"F7.opExtrude","CAP_EDGE",EDGE,{"disambiguationData":[OSD([sQuery(id+"F6.wireOp",EDGE,"E34.filletArc")])],"isStart":false});
            var Q125;
            Q125=makeQuery(id+"F7.opExtrude","CAP_EDGE",EDGE,{"disambiguationData":[OSD([sQuery(id+"F6.wireOp",EDGE,"E40.1.16")])],"isStart":false});
            var Q126;
            Q126=makeQuery(id+"F10.opExtrude","CAP_EDGE",EDGE,{"disambiguationData":[OSD([sQuery(id+"F9.wireOp",EDGE,"E41.bottom")])],"isStart":true});
            var Q127;
            Q127=makeQuery(id+"F1.opExtrude","CAP_EDGE",EDGE,{"disambiguationData":[OSD([sQuery(id+"F0.wireOp",EDGE,"E11.1.0")])],"isStart":false});
            var Q128;
            Q128=makeQuery(id+"F4.opExtrude","CAP_EDGE",EDGE,{"disambiguationData":[OSD([sQuery(id+"F3.wireOp",EDGE,"E19.0")])],"isStart":true});
            var Q129;
            Q129=makeQuery(id+"F4.opExtrude","CAP_EDGE",EDGE,{"disambiguationData":[OSD([sQuery(id+"F3.wireOp",EDGE,"E25.2.0")])],"isStart":true});
            var Q130;
            Q130=makeQuery(id+"F10.opExtrude","CAP_EDGE",EDGE,{"disambiguationData":[OSD([sQuery(id+"F9.wireOp",EDGE,"E49.right")])],"isStart":true});
            var Q131;
            {var subQ0=sQuery(id+"F9.wireOp",EDGE,"E45.left");Q131=qUnion([makeQuery(id+"F11.opPattern","COPY",EDGE,{"derivedFrom":makeQuery(id+"F10.opExtrude","SWEPT_EDGE",EDGE,{"disambiguationData":[OSD([sQuery(id+"F9.wireOp",EDGE,"E45.top"),subQ0])]}),"instanceName":"2"}),makeQuery(id+"F11.opPattern","COPY",EDGE,{"derivedFrom":makeQuery(id+"F10.opExtrude","SWEPT_EDGE",EDGE,{"disambiguationData":[OSD([subQ0,sQuery(id+"F9.wireOp",EDGE,"E53")])]}),"instanceName":"2"})]);}
            var Q132;
            Q132=makeQuery(id+"F11.opPattern","COPY",EDGE,{"derivedFrom":makeQuery(id+"F10.opExtrude","CAP_EDGE",EDGE,{"disambiguationData":[OSD([sQuery(id+"F9.wireOp",EDGE,"E46.right")])],"isStart":true}),"instanceName":"1"});
            var Q133;
            Q133=makeQuery(id+"F4.opExtrude","CAP_EDGE",EDGE,{"disambiguationData":[OSD([sQuery(id+"F3.wireOp",EDGE,"E21.0")])],"isStart":false});
            var Q134;
            Q134=makeQuery(id+"F4.opExtrude","CAP_EDGE",EDGE,{"disambiguationData":[OSD([sQuery(id+"F3.wireOp",EDGE,"E12.0")])],"isStart":false});
            var Q135;
            Q135=makeQuery(id+"F11.opPattern","COPY",EDGE,{"derivedFrom":makeQuery(id+"F10.opExtrude","CAP_EDGE",EDGE,{"disambiguationData":[OSD([sQuery(id+"F9.wireOp",EDGE,"E46.right")])],"isStart":true}),"instanceName":"2"});
            var Q136;
            Q136=makeQuery(id+"F7.opExtrude","CAP_EDGE",EDGE,{"disambiguationData":[OSD([sQuery(id+"F6.wireOp",EDGE,"E40.1.7")])],"isStart":true});
            var Q137;
            Q137=makeQuery(id+"F7.opExtrude","CAP_EDGE",EDGE,{"disambiguationData":[OSD([sQuery(id+"F6.wireOp",EDGE,"E35")])],"isStart":true});
            var Q138;
            Q138=makeQuery(id+"F10.opExtrude","CAP_EDGE",EDGE,{"disambiguationData":[OSD([sQuery(id+"F9.wireOp",EDGE,"E46.bottom")])],"isStart":false});
            var Q139;
            Q139=makeQuery(id+"F11.opPattern","COPY",EDGE,{"derivedFrom":makeQuery(id+"F10.opExtrude","CAP_EDGE",EDGE,{"disambiguationData":[OSD([sQuery(id+"F9.wireOp",EDGE,"E41.left")])],"isStart":false}),"instanceName":"1"});
            var Q140;
            Q140=makeQuery(id+"F11.opPattern","COPY",EDGE,{"derivedFrom":makeQuery(id+"F10.opExtrude","CAP_EDGE",EDGE,{"disambiguationData":[OSD([sQuery(id+"F9.wireOp",EDGE,"E46.right")])],"isStart":false}),"instanceName":"1"});
            var Q141;
            Q141=makeQuery(id+"F11.opPattern","COPY",EDGE,{"derivedFrom":makeQuery(id+"F10.opExtrude","CAP_EDGE",EDGE,{"disambiguationData":[OSD([sQuery(id+"F9.wireOp",EDGE,"E41.left")])],"isStart":false}),"instanceName":"2"});
            var Q142;
            Q142=makeQuery(id+"F11.opPattern","COPY",EDGE,{"derivedFrom":makeQuery(id+"F10.opExtrude","CAP_EDGE",EDGE,{"disambiguationData":[OSD([sQuery(id+"F9.wireOp",EDGE,"E46.right")])],"isStart":false}),"instanceName":"2"});
            var Q143;
            Q143=makeQuery(id+"F1.opExtrude","CAP_EDGE",EDGE,{"disambiguationData":[OSD([sQuery(id+"F0.wireOp",EDGE,"E10")])],"isStart":false});
            var Q144;
            Q144=makeQuery(id+"F7.opExtrude","CAP_EDGE",EDGE,{"disambiguationData":[OSD([sQuery(id+"F6.wireOp",EDGE,"E40.2.12")])],"isStart":true});
            var Q145;
            Q145=makeQuery(id+"F7.opExtrude","CAP_EDGE",EDGE,{"disambiguationData":[OSD([sQuery(id+"F6.wireOp",EDGE,"E40.1.6")])],"isStart":true});
            var Q146;
            Q146=makeQuery(id+"F7.opExtrude","CAP_EDGE",EDGE,{"disambiguationData":[OSD([sQuery(id+"F6.wireOp",EDGE,"E40.1.7")])],"isStart":false});
            var Q147;
            Q147=makeQuery(id+"F7.opExtrude","CAP_EDGE",EDGE,{"disambiguationData":[OSD([sQuery(id+"F6.wireOp",EDGE,"E35")])],"isStart":false});
            var Q148;
            Q148=makeQuery(id+"F10.opExtrude","CAP_EDGE",EDGE,{"disambiguationData":[OSD([sQuery(id+"F9.wireOp",EDGE,"E50.bottom")])],"isStart":false});
            var Q149;
            Q149=makeQuery(id+"F11.opPattern","COPY",EDGE,{"derivedFrom":makeQuery(id+"F10.opExtrude","CAP_EDGE",EDGE,{"disambiguationData":[OSD([sQuery(id+"F9.wireOp",EDGE,"E41.left")])],"isStart":true}),"instanceName":"1"});
            var Q150;
            Q150=makeQuery(id+"F11.opPattern","COPY",EDGE,{"derivedFrom":makeQuery(id+"F10.opExtrude","CAP_EDGE",EDGE,{"disambiguationData":[OSD([sQuery(id+"F9.wireOp",EDGE,"E41.left")])],"isStart":true}),"instanceName":"2"});
            var Q151;
            Q151=makeQuery(id+"F4.opExtrude","CAP_EDGE",EDGE,{"disambiguationData":[OSD([sQuery(id+"F3.wireOp",EDGE,"E20.1.0")])],"isStart":true});
            var Q152;
            Q152=makeQuery(id+"F1.opExtrude","CAP_EDGE",EDGE,{"disambiguationData":[OSD([sQuery(id+"F0.wireOp",EDGE,"E11.1.0")])],"isStart":true});
            var Q153;
            Q153=makeQuery(id+"F7.opExtrude","CAP_EDGE",EDGE,{"disambiguationData":[OSD([sQuery(id+"F6.wireOp",EDGE,"E33.filletArc")])],"isStart":false});
            var Q154;
            Q154=makeQuery(id+"F4.opExtrude","CAP_EDGE",EDGE,{"disambiguationData":[OSD([sQuery(id+"F3.wireOp",EDGE,"E21.0")])],"isStart":true});
            var Q155;
            Q155=makeQuery(id+"F7.opExtrude","CAP_EDGE",EDGE,{"disambiguationData":[OSD([sQuery(id+"F6.wireOp",EDGE,"E40.2.11")])],"isStart":false});
            var Q156;
            Q156=makeQuery(id+"F7.opExtrude","CAP_EDGE",EDGE,{"disambiguationData":[OSD([sQuery(id+"F6.wireOp",EDGE,"E40.1.15")])],"isStart":false});
            var Q157;
            Q157=makeQuery(id+"F7.opExtrude","CAP_EDGE",EDGE,{"disambiguationData":[OSD([sQuery(id+"F6.wireOp",EDGE,"E40.1.5")])],"isStart":false});
            var Q158;
            Q158=makeQuery(id+"F7.opExtrude","SWEPT_EDGE",EDGE,{"disambiguationData":[OSD([sQuery(id+"F6.wireOp",EDGE,"E30.2"),sQuery(id+"F6.wireOp",EDGE,"E33.filletArc")])]});
            var Q159;
            Q159=makeQuery(id+"F11.opPattern","COPY",EDGE,{"derivedFrom":makeQuery(id+"F10.opExtrude","CAP_EDGE",EDGE,{"disambiguationData":[OSD([sQuery(id+"F9.wireOp",EDGE,"E46.bottom")])],"isStart":true}),"instanceName":"2"});
            var Q160;
            Q160=makeQuery(id+"F7.opExtrude","SWEPT_EDGE",EDGE,{"disambiguationData":[OSD([sQuery(id+"F6.wireOp",EDGE,"E40.1.1"),sQuery(id+"F6.wireOp",EDGE,"E40.1.16")])]});
            var Q161;
            Q161=makeQuery(id+"F7.opExtrude","SWEPT_EDGE",EDGE,{"disambiguationData":[OSD([sQuery(id+"F6.wireOp",EDGE,"E40.1.1"),sQuery(id+"F6.wireOp",EDGE,"E40.1.10")])]});
            var Q162;
            Q162=makeQuery(id+"F7.opExtrude","SWEPT_EDGE",EDGE,{"disambiguationData":[OSD([sQuery(id+"F6.wireOp",EDGE,"E30.0"),sQuery(id+"F6.wireOp",EDGE,"E32.filletArc")])]});
            var Q163;
            Q163=makeQuery(id+"F11.opPattern","COPY",EDGE,{"derivedFrom":makeQuery(id+"F10.opExtrude","CAP_EDGE",EDGE,{"disambiguationData":[OSD([sQuery(id+"F9.wireOp",EDGE,"E46.bottom")])],"isStart":true}),"instanceName":"1"});
            var Q164;
            {var subQ0=sQuery(id+"F9.wireOp",EDGE,"E41.bottom");Q164=qUnion([makeQuery(id+"F11.opPattern","COPY",EDGE,{"derivedFrom":makeQuery(id+"F10.opExtrude","SWEPT_EDGE",EDGE,{"disambiguationData":[OSD([subQ0,sQuery(id+"F9.wireOp",EDGE,"E49.right")])]}),"instanceName":"2"}),makeQuery(id+"F11.opPattern","COPY",EDGE,{"derivedFrom":makeQuery(id+"F10.opExtrude","SWEPT_EDGE",EDGE,{"disambiguationData":[OSD([subQ0,sQuery(id+"F9.wireOp",EDGE,"E48.right")])]}),"instanceName":"2"})]);}
            var Q165;
            Q165=makeQuery(id+"F7.opExtrude","SWEPT_EDGE",EDGE,{"disambiguationData":[OSD([sQuery(id+"F6.wireOp",EDGE,"E30.1"),sQuery(id+"F6.wireOp",EDGE,"E34.filletArc")])]});
            var Q166;
            Q166=makeQuery(id+"F7.opExtrude","SWEPT_EDGE",EDGE,{"disambiguationData":[OSD([sQuery(id+"F6.wireOp",EDGE,"E30.2"),sQuery(id+"F6.wireOp",EDGE,"E32.filletArc")])]});
            var Q167;
            Q167=makeQuery(id+"F7.opExtrude","SWEPT_EDGE",EDGE,{"disambiguationData":[OSD([sQuery(id+"F6.wireOp",EDGE,"E40.2.1"),sQuery(id+"F6.wireOp",EDGE,"E40.2.16")])]});
            var Q168;
            Q168=makeQuery(id+"F10.opExtrude","CAP_EDGE",EDGE,{"disambiguationData":[OSD([sQuery(id+"F9.wireOp",EDGE,"E46.right")])],"isStart":true});
            var Q169;
            Q169=makeQuery(id+"F7.opExtrude","CAP_EDGE",EDGE,{"disambiguationData":[OSD([sQuery(id+"F6.wireOp",EDGE,"E40.2.15")])],"isStart":true});
            var Q170;
            Q170=makeQuery(id+"F7.opExtrude","CAP_EDGE",EDGE,{"disambiguationData":[OSD([sQuery(id+"F6.wireOp",EDGE,"E40.2.5")])],"isStart":true});
            var Q171;
            Q171=makeQuery(id+"F7.opExtrude","CAP_EDGE",EDGE,{"disambiguationData":[OSD([sQuery(id+"F6.wireOp",EDGE,"E40.1.8")])],"isStart":true});
            var Q172;
            Q172=makeQuery(id+"F7.opExtrude","CAP_EDGE",EDGE,{"disambiguationData":[OSD([sQuery(id+"F6.wireOp",EDGE,"E36.0.MirrorC")])],"isStart":true});
            var Q173;
            Q173=makeQuery(id+"F7.opExtrude","SWEPT_EDGE",EDGE,{"disambiguationData":[OSD([sQuery(id+"F6.wireOp",EDGE,"E40.2.6"),sQuery(id+"F6.wireOp",EDGE,"E40.2.16")])]});
            var Q174;
            Q174=makeQuery(id+"F7.opExtrude","SWEPT_EDGE",EDGE,{"disambiguationData":[OSD([sQuery(id+"F6.wireOp",EDGE,"E40.1.5"),sQuery(id+"F6.wireOp",EDGE,"E40.1.12")])]});
            var Q175;
            Q175=makeQuery(id+"F7.opExtrude","SWEPT_EDGE",EDGE,{"disambiguationData":[OSD([sQuery(id+"F6.wireOp",EDGE,"E40.1.5"),sQuery(id+"F6.wireOp",EDGE,"E40.1.6")])]});
            var Q176;
            Q176=makeQuery(id+"F7.opExtrude","SWEPT_EDGE",EDGE,{"disambiguationData":[OSD([sQuery(id+"F6.wireOp",EDGE,"E40.1.10"),sQuery(id+"F6.wireOp",EDGE,"E40.1.12")])]});
            var Q177;
            Q177=makeQuery(id+"F7.opExtrude","SWEPT_EDGE",EDGE,{"disambiguationData":[OSD([sQuery(id+"F6.wireOp",EDGE,"E40.2.5"),sQuery(id+"F6.wireOp",EDGE,"E40.2.6")])]});
            var Q178;
            Q178=makeQuery(id+"F7.opExtrude","SWEPT_EDGE",EDGE,{"disambiguationData":[OSD([sQuery(id+"F6.wireOp",EDGE,"E40.2.5"),sQuery(id+"F6.wireOp",EDGE,"E40.2.12")])]});
            var Q179;
            Q179=makeQuery(id+"F7.opExtrude","SWEPT_EDGE",EDGE,{"disambiguationData":[OSD([sQuery(id+"F6.wireOp",EDGE,"E40.2.1"),sQuery(id+"F6.wireOp",EDGE,"E40.2.10")])]});
            var Q180;
            Q180=makeQuery(id+"F4.opExtrude","SWEPT_EDGE",EDGE,{"disambiguationData":[OSD([sQuery(id+"F3.wireOp",EDGE,"E20.1.0"),sQuery(id+"F3.wireOp",EDGE,"E20.1.1")])]});
            var Q181;
            Q181=makeQuery(id+"F4.opExtrude","CAP_EDGE",EDGE,{"disambiguationData":[OSD([sQuery(id+"F3.wireOp",EDGE,"E20.1.1")])],"isStart":true});
            var Q182;
            Q182=makeQuery(id+"F4.opExtrude","SWEPT_EDGE",EDGE,{"disambiguationData":[OSD([sQuery(id+"F3.wireOp",EDGE,"E18.1.MirrorCS"),sQuery(id+"F3.wireOp",EDGE,"E19.0")])]});
            var Q183;
            Q183=makeQuery(id+"F4.opExtrude","SWEPT_EDGE",EDGE,{"disambiguationData":[OSD([sQuery(id+"F3.wireOp",EDGE,"E16"),sQuery(id+"F3.wireOp",EDGE,"E20.1.4")])]});
            var Q184;
            Q184=makeQuery(id+"F4.opExtrude","SWEPT_EDGE",EDGE,{"disambiguationData":[OSD([sQuery(id+"F3.wireOp",EDGE,"E14"),sQuery(id+"F3.wireOp",EDGE,"E19.0")])]});
            var Q185;
            Q185=makeQuery(id+"F1.opExtrude","CAP_EDGE",EDGE,{"disambiguationData":[OSD([sQuery(id+"F0.wireOp",EDGE,"E10")])],"isStart":true});
            var Q186;
            Q186=makeQuery(id+"F10.opExtrude","CAP_EDGE",EDGE,{"disambiguationData":[OSD([sQuery(id+"F9.wireOp",EDGE,"E46.right")])],"isStart":false});
            var Q187;
            Q187=makeQuery(id+"F7.opExtrude","CAP_EDGE",EDGE,{"disambiguationData":[OSD([sQuery(id+"F6.wireOp",EDGE,"E40.2.5")])],"isStart":false});
            var Q188;
            Q188=makeQuery(id+"F7.opExtrude","CAP_EDGE",EDGE,{"disambiguationData":[OSD([sQuery(id+"F6.wireOp",EDGE,"E40.2.15")])],"isStart":false});
            var Q189;
            Q189=makeQuery(id+"F10.opExtrude","CAP_EDGE",EDGE,{"disambiguationData":[OSD([sQuery(id+"F9.wireOp",EDGE,"E41.left")])],"isStart":false});
            var Q190;
            Q190=makeQuery(id+"F7.opExtrude","CAP_EDGE",EDGE,{"disambiguationData":[OSD([sQuery(id+"F6.wireOp",EDGE,"E36.0.MirrorC")])],"isStart":false});
            var Q191;
            Q191=makeQuery(id+"F7.opExtrude","CAP_EDGE",EDGE,{"disambiguationData":[OSD([sQuery(id+"F6.wireOp",EDGE,"E40.1.8")])],"isStart":false});
            var Q192;
            Q192=makeQuery(id+"F7.opExtrude","SWEPT_EDGE",EDGE,{"disambiguationData":[OSD([sQuery(id+"F6.wireOp",EDGE,"E40.2.10"),sQuery(id+"F6.wireOp",EDGE,"E40.2.12")])]});
            var Q193;
            Q193=makeQuery(id+"F4.opExtrude","SWEPT_EDGE",EDGE,{"disambiguationData":[OSD([sQuery(id+"F3.wireOp",EDGE,"E20.2.1"),sQuery(id+"F3.wireOp",EDGE,"E20.2.2")])]});
            var Q194;
            Q194=makeQuery(id+"F4.opExtrude","SWEPT_EDGE",EDGE,{"disambiguationData":[OSD([sQuery(id+"F3.wireOp",EDGE,"E20.1.2"),sQuery(id+"F3.wireOp",EDGE,"E20.1.3")])]});
            var Q195;
            Q195=makeQuery(id+"F4.opExtrude","SWEPT_EDGE",EDGE,{"disambiguationData":[OSD([sQuery(id+"F3.wireOp",EDGE,"E20.1.0"),sQuery(id+"F3.wireOp",EDGE,"E20.2.4")])]});
            var Q196;
            Q196=makeQuery(id+"F4.opExtrude","SWEPT_EDGE",EDGE,{"disambiguationData":[OSD([sQuery(id+"F3.wireOp",EDGE,"E20.1.1"),sQuery(id+"F3.wireOp",EDGE,"E20.1.2")])]});
            var Q197;
            Q197=makeQuery(id+"F4.opExtrude","CAP_EDGE",EDGE,{"disambiguationData":[OSD([sQuery(id+"F3.wireOp",EDGE,"E12.0")])],"isStart":true});
            var Q198;
            Q198=makeQuery(id+"F4.opExtrude","SWEPT_EDGE",EDGE,{"disambiguationData":[OSD([sQuery(id+"F3.wireOp",EDGE,"E20.2.3"),sQuery(id+"F3.wireOp",EDGE,"E20.2.4")])]});
            var Q199;
            Q199=makeQuery(id+"F4.opExtrude","SWEPT_EDGE",EDGE,{"disambiguationData":[OSD([sQuery(id+"F3.wireOp",EDGE,"E20.2.2"),sQuery(id+"F3.wireOp",EDGE,"E20.2.3")])]});
            var Q200;
            {var subQ0=sQuery(id+"F9.wireOp",EDGE,"E41.left");var subQ1=sQuery(id+"F9.wireOp",EDGE,"E46.bottom");Q200=qUnion([makeQuery(id+"F11.opPattern","COPY",EDGE,{"derivedFrom":makeQuery(id+"F10.opExtrude","SWEPT_EDGE",EDGE,{"disambiguationData":[OSD([subQ0,sQuery(id+"F9.wireOp",EDGE,"E48.top")])]}),"instanceName":"2"}),makeQuery(id+"F11.opPattern","COPY",EDGE,{"derivedFrom":makeQuery(id+"F10.opExtrude","SWEPT_EDGE",EDGE,{"disambiguationData":[OSD([subQ0,sQuery(id+"F9.wireOp",EDGE,"E45.top")])]}),"instanceName":"2"}),makeQuery(id+"F11.opPattern","COPY",EDGE,{"derivedFrom":makeQuery(id+"F10.opExtrude","SWEPT_EDGE",EDGE,{"disambiguationData":[OSD([subQ1,sQuery(id+"F9.wireOp",EDGE,"E51.trimOffspring")])]}),"instanceName":"2"}),makeQuery(id+"F11.opPattern","COPY",EDGE,{"derivedFrom":makeQuery(id+"F10.opExtrude","SWEPT_EDGE",EDGE,{"disambiguationData":[OSD([subQ1,sQuery(id+"F9.wireOp",EDGE,"E46.right")])]}),"instanceName":"2"})]);}
            var Q201;
            Q201=makeQuery(id+"F7.opExtrude","CAP_EDGE",EDGE,{"disambiguationData":[OSD([sQuery(id+"F6.wireOp",EDGE,"E37")])],"isStart":true});
            var Q202;
            Q202=makeQuery(id+"F7.opExtrude","CAP_EDGE",EDGE,{"disambiguationData":[OSD([sQuery(id+"F6.wireOp",EDGE,"E40.1.10")])],"isStart":true});
            var Q203;
            Q203=makeQuery(id+"F1.opExtrude","SWEPT_EDGE",EDGE,{"disambiguationData":[OSD([sQuery(id+"F0.wireOp",EDGE,"E0"),sQuery(id+"F0.wireOp",EDGE,"E1.2")])]});
            var Q204;
            Q204=makeQuery(id+"F1.opExtrude","SWEPT_EDGE",EDGE,{"disambiguationData":[OSD([sQuery(id+"F0.wireOp",EDGE,"E0"),sQuery(id+"F0.wireOp",EDGE,"E1.1")])]});
            var Q205;
            Q205=makeQuery(id+"F10.opExtrude","CAP_EDGE",EDGE,{"disambiguationData":[OSD([sQuery(id+"F9.wireOp",EDGE,"E46.top")])],"isStart":true});
            var Q206;
            Q206=makeQuery(id+"F11.opPattern","COPY",EDGE,{"derivedFrom":makeQuery(id+"F10.opExtrude","CAP_EDGE",EDGE,{"disambiguationData":[OSD([sQuery(id+"F9.wireOp",EDGE,"E46.top")])],"isStart":true}),"instanceName":"2"});
            var Q207;
            Q207=makeQuery(id+"F10.opExtrude","CAP_EDGE",EDGE,{"disambiguationData":[OSD([sQuery(id+"F9.wireOp",EDGE,"E41.left")])],"isStart":true});
            var Q208;
            Q208=makeQuery(id+"F1.opExtrude","SWEPT_EDGE",EDGE,{"disambiguationData":[OSD([sQuery(id+"F0.wireOp",EDGE,"E1.0"),sQuery(id+"F0.wireOp",EDGE,"E5.trimOffspring")])]});
            var Q209;
            Q209=makeQuery(id+"F1.opExtrude","SWEPT_EDGE",EDGE,{"disambiguationData":[OSD([sQuery(id+"F0.wireOp",EDGE,"E1.1"),sQuery(id+"F0.wireOp",EDGE,"E5.trimOffspring")])]});
            var Q210;
            Q210=makeQuery(id+"F1.opExtrude","CAP_EDGE",EDGE,{"disambiguationData":[OSD([sQuery(id+"F0.wireOp",EDGE,"E0")])],"isStart":false});
            var Q211;
            Q211=makeQuery(id+"F1.opExtrude","CAP_EDGE",EDGE,{"disambiguationData":[OSD([sQuery(id+"F0.wireOp",EDGE,"E1.0")])],"isStart":true});
            var Q212;
            Q212=makeQuery(id+"F1.opExtrude","CAP_EDGE",EDGE,{"disambiguationData":[OSD([sQuery(id+"F0.wireOp",EDGE,"E9.1.0")])],"isStart":false});
            var Q213;
            Q213=makeQuery(id+"F1.opExtrude","CAP_EDGE",EDGE,{"disambiguationData":[OSD([sQuery(id+"F0.wireOp",EDGE,"E1.2")])],"isStart":true});
            var Q214;
            Q214=makeQuery(id+"F7.opExtrude","CAP_EDGE",EDGE,{"disambiguationData":[OSD([sQuery(id+"F6.wireOp",EDGE,"E40.2.16")])],"isStart":true});
            var Q215;
            Q215=makeQuery(id+"F7.opExtrude","CAP_EDGE",EDGE,{"disambiguationData":[OSD([sQuery(id+"F6.wireOp",EDGE,"E40.2.6")])],"isStart":true});
            var Q216;
            Q216=makeQuery(id+"F1.opExtrude","CAP_EDGE",EDGE,{"disambiguationData":[OSD([sQuery(id+"F0.wireOp",EDGE,"E1.2")])],"isStart":false});
            var Q217;
            Q217=makeQuery(id+"F11.opPattern","COPY",EDGE,{"derivedFrom":makeQuery(id+"F10.opExtrude","CAP_EDGE",EDGE,{"disambiguationData":[OSD([sQuery(id+"F9.wireOp",EDGE,"E41.bottom")])],"isStart":false}),"instanceName":"2"});
            var Q218;
            Q218=makeQuery(id+"F11.opPattern","COPY",EDGE,{"derivedFrom":makeQuery(id+"F10.opExtrude","CAP_EDGE",EDGE,{"disambiguationData":[OSD([sQuery(id+"F9.wireOp",EDGE,"E46.bottom")])],"isStart":false}),"instanceName":"1"});
            var Q219;
            Q219=makeQuery(id+"F7.opExtrude","CAP_EDGE",EDGE,{"disambiguationData":[OSD([sQuery(id+"F6.wireOp",EDGE,"E40.2.16")])],"isStart":false});
            var Q220;
            Q220=makeQuery(id+"F7.opExtrude","CAP_EDGE",EDGE,{"disambiguationData":[OSD([sQuery(id+"F6.wireOp",EDGE,"E40.1.10")])],"isStart":false});
            var Q221;
            Q221=makeQuery(id+"F7.opExtrude","CAP_EDGE",EDGE,{"disambiguationData":[OSD([sQuery(id+"F6.wireOp",EDGE,"E37")])],"isStart":false});
            var Q222;
            Q222=makeQuery(id+"F1.opExtrude","CAP_EDGE",EDGE,{"disambiguationData":[OSD([sQuery(id+"F0.wireOp",EDGE,"E9.2.0")])],"isStart":true});
            var Q223;
            Q223=makeQuery(id+"F10.opExtrude","CAP_EDGE",EDGE,{"disambiguationData":[OSD([sQuery(id+"F9.wireOp",EDGE,"E41.left")])],"isStart":false});
            var Q224;
            Q224=makeQuery(id+"F7.opExtrude","CAP_EDGE",EDGE,{"disambiguationData":[OSD([sQuery(id+"F6.wireOp",EDGE,"E40.2.7")])],"isStart":true});
            var Q225;
            Q225=makeQuery(id+"F11.opPattern","COPY",EDGE,{"derivedFrom":makeQuery(id+"F10.opExtrude","CAP_EDGE",EDGE,{"disambiguationData":[OSD([sQuery(id+"F9.wireOp",EDGE,"E50.bottom")])],"isStart":true}),"instanceName":"1"});
            var Q226;
            Q226=makeQuery(id+"F7.opExtrude","CAP_EDGE",EDGE,{"disambiguationData":[OSD([sQuery(id+"F6.wireOp",EDGE,"E30.1")])],"isStart":true});
            var Q227;
            Q227=makeQuery(id+"F7.opExtrude","CAP_EDGE",EDGE,{"disambiguationData":[OSD([sQuery(id+"F6.wireOp",EDGE,"E38")])],"isStart":true});
            var Q228;
            Q228=makeQuery(id+"F7.opExtrude","CAP_EDGE",EDGE,{"disambiguationData":[OSD([sQuery(id+"F6.wireOp",EDGE,"E40.1.11")])],"isStart":true});
            var Q229;
            Q229=makeQuery(id+"F11.opPattern","COPY",EDGE,{"derivedFrom":makeQuery(id+"F10.opExtrude","CAP_EDGE",EDGE,{"disambiguationData":[OSD([sQuery(id+"F9.wireOp",EDGE,"E45.bottom")])],"isStart":true}),"instanceName":"2"});
            var Q230;
            Q230=makeQuery(id+"F7.opExtrude","CAP_EDGE",EDGE,{"disambiguationData":[OSD([sQuery(id+"F6.wireOp",EDGE,"E40.1.11")])],"isStart":false});
            var Q231;
            Q231=makeQuery(id+"F7.opExtrude","CAP_EDGE",EDGE,{"disambiguationData":[OSD([sQuery(id+"F6.wireOp",EDGE,"E38")])],"isStart":false});
            var Q232;
            Q232=makeQuery(id+"F7.opExtrude","CAP_EDGE",EDGE,{"disambiguationData":[OSD([sQuery(id+"F6.wireOp",EDGE,"E40.2.7")])],"isStart":false});
            var Q233;
            Q233=makeQuery(id+"F11.opPattern","COPY",EDGE,{"derivedFrom":makeQuery(id+"F10.opExtrude","CAP_EDGE",EDGE,{"disambiguationData":[OSD([sQuery(id+"F9.wireOp",EDGE,"E50.bottom")])],"isStart":false}),"instanceName":"1"});
            var Q234;
            Q234=makeQuery(id+"F11.opPattern","COPY",EDGE,{"derivedFrom":makeQuery(id+"F10.opExtrude","CAP_EDGE",EDGE,{"disambiguationData":[OSD([sQuery(id+"F9.wireOp",EDGE,"E45.bottom")])],"isStart":false}),"instanceName":"1"});
            var Q235;
            Q235=makeQuery(id+"F10.opExtrude","CAP_EDGE",EDGE,{"disambiguationData":[OSD([sQuery(id+"F9.wireOp",EDGE,"E41.left")])],"isStart":false});
            var Q236;
            {var subQ0=sQuery(id+"F9.wireOp",EDGE,"E41.left");var subQ1=sQuery(id+"F9.wireOp",EDGE,"E50.top");Q236=qUnion([makeQuery(id+"F11.opPattern","COPY",EDGE,{"derivedFrom":makeQuery(id+"F10.opExtrude","SWEPT_EDGE",EDGE,{"disambiguationData":[OSD([subQ0,sQuery(id+"F9.wireOp",EDGE,"E48.top")])]}),"instanceName":"2"}),makeQuery(id+"F11.opPattern","COPY",EDGE,{"derivedFrom":makeQuery(id+"F10.opExtrude","SWEPT_EDGE",EDGE,{"disambiguationData":[OSD([subQ0,sQuery(id+"F9.wireOp",EDGE,"E45.top")])]}),"instanceName":"2"}),makeQuery(id+"F11.opPattern","COPY",EDGE,{"derivedFrom":makeQuery(id+"F10.opExtrude","SWEPT_EDGE",EDGE,{"disambiguationData":[OSD([subQ1,sQuery(id+"F9.wireOp",EDGE,"E50.left")])]}),"instanceName":"2"}),makeQuery(id+"F11.opPattern","COPY",EDGE,{"derivedFrom":makeQuery(id+"F10.opExtrude","SWEPT_EDGE",EDGE,{"disambiguationData":[OSD([subQ1,sQuery(id+"F9.wireOp",EDGE,"E51.trimOffspring")])]}),"instanceName":"2"})]);}
            var Q237;
            Q237=makeQuery(id+"F11.opPattern","COPY",EDGE,{"derivedFrom":makeQuery(id+"F10.opExtrude","CAP_EDGE",EDGE,{"disambiguationData":[OSD([sQuery(id+"F9.wireOp",EDGE,"E50.left")])],"isStart":false}),"instanceName":"1"});
            var Q238;
            Q238=makeQuery(id+"F10.opExtrude","CAP_EDGE",EDGE,{"disambiguationData":[OSD([sQuery(id+"F9.wireOp",EDGE,"E41.left")])],"isStart":true});
            var Q239;
            Q239=makeQuery(id+"F11.opPattern","COPY",EDGE,{"derivedFrom":makeQuery(id+"F10.opExtrude","CAP_EDGE",EDGE,{"disambiguationData":[OSD([sQuery(id+"F9.wireOp",EDGE,"E50.left")])],"isStart":false}),"instanceName":"2"});
            var Q240;
            Q240=makeQuery(id+"F10.opExtrude","CAP_EDGE",EDGE,{"disambiguationData":[OSD([sQuery(id+"F9.wireOp",EDGE,"E48.top")])],"isStart":true});
            var Q241;
            Q241=makeQuery(id+"F11.opPattern","COPY",EDGE,{"derivedFrom":makeQuery(id+"F10.opExtrude","CAP_EDGE",EDGE,{"disambiguationData":[OSD([sQuery(id+"F9.wireOp",EDGE,"E50.top")])],"isStart":true}),"instanceName":"2"});
            var Q242;
            Q242=makeQuery(id+"F11.opPattern","COPY",EDGE,{"derivedFrom":makeQuery(id+"F10.opExtrude","CAP_EDGE",EDGE,{"disambiguationData":[OSD([sQuery(id+"F9.wireOp",EDGE,"E45.top")])],"isStart":true}),"instanceName":"2"});
            var Q243;
            Q243=makeQuery(id+"F7.opExtrude","CAP_EDGE",EDGE,{"disambiguationData":[OSD([sQuery(id+"F6.wireOp",EDGE,"E40.2.8")])],"isStart":true});
            var Q244;
            Q244=makeQuery(id+"F11.opPattern","COPY",EDGE,{"derivedFrom":makeQuery(id+"F10.opExtrude","CAP_EDGE",EDGE,{"disambiguationData":[OSD([sQuery(id+"F9.wireOp",EDGE,"E45.top")])],"isStart":true}),"instanceName":"1"});
            var Q245;
            Q245=makeQuery(id+"F7.opExtrude","CAP_EDGE",EDGE,{"disambiguationData":[OSD([sQuery(id+"F6.wireOp",EDGE,"E40.1.12")])],"isStart":true});
            var Q246;
            Q246=makeQuery(id+"F7.opExtrude","CAP_EDGE",EDGE,{"disambiguationData":[OSD([sQuery(id+"F6.wireOp",EDGE,"E39.0.MirrorC")])],"isStart":true});
            var Q247;
            Q247=makeQuery(id+"F1.opExtrude","CAP_EDGE",EDGE,{"disambiguationData":[OSD([sQuery(id+"F0.wireOp",EDGE,"E8")])],"isStart":true});
            var Q248;
            Q248=makeQuery(id+"F11.opPattern","COPY",EDGE,{"derivedFrom":makeQuery(id+"F10.opExtrude","CAP_EDGE",EDGE,{"disambiguationData":[OSD([sQuery(id+"F9.wireOp",EDGE,"E50.left")])],"isStart":true}),"instanceName":"1"});
            var Q249;
            {var subQ0=sQuery(id+"F9.wireOp",EDGE,"E48.right");Q249=qUnion([makeQuery(id+"F10.opExtrude","SWEPT_EDGE",EDGE,{"disambiguationData":[OSD([sQuery(id+"F9.wireOp",EDGE,"E41.bottom"),subQ0])]}),makeQuery(id+"F10.opExtrude","SWEPT_EDGE",EDGE,{"disambiguationData":[OSD([sQuery(id+"F9.wireOp",EDGE,"E48.top"),subQ0])]})]);}
            var Q250;
            Q250=makeQuery(id+"F11.opPattern","COPY",EDGE,{"derivedFrom":makeQuery(id+"F10.opExtrude","SWEPT_EDGE",EDGE,{"disambiguationData":[OSD([sQuery(id+"F9.wireOp",EDGE,"E48.top"),sQuery(id+"F9.wireOp",EDGE,"E48.right")])]}),"instanceName":"1"});
            var Q251;
            Q251=makeQuery(id+"F11.opPattern","COPY",EDGE,{"derivedFrom":makeQuery(id+"F10.opExtrude","SWEPT_EDGE",EDGE,{"disambiguationData":[OSD([sQuery(id+"F9.wireOp",EDGE,"E41.left"),sQuery(id+"F9.wireOp",EDGE,"E48.top")])]}),"instanceName":"1"});
            var Q252;
            {var subQ0=sQuery(id+"F9.wireOp",EDGE,"E41.bottom");Q252=qUnion([makeQuery(id+"F11.opPattern","COPY",EDGE,{"derivedFrom":makeQuery(id+"F10.opExtrude","SWEPT_EDGE",EDGE,{"disambiguationData":[OSD([subQ0,sQuery(id+"F9.wireOp",EDGE,"E49.right")])]}),"instanceName":"1"}),makeQuery(id+"F11.opPattern","COPY",EDGE,{"derivedFrom":makeQuery(id+"F10.opExtrude","SWEPT_EDGE",EDGE,{"disambiguationData":[OSD([subQ0,sQuery(id+"F9.wireOp",EDGE,"E48.right")])]}),"instanceName":"1"})]);}
            var Q253;
            Q253=makeQuery(id+"F4.opExtrude","CAP_EDGE",EDGE,{"disambiguationData":[OSD([sQuery(id+"F3.wireOp",EDGE,"E24")])],"isStart":false});
            var Q254;
            Q254=makeQuery(id+"F10.opExtrude","CAP_EDGE",EDGE,{"disambiguationData":[OSD([sQuery(id+"F9.wireOp",EDGE,"E45.left")])],"isStart":true});
            var Q255;
            Q255=makeQuery(id+"F10.opExtrude","CAP_EDGE",EDGE,{"disambiguationData":[OSD([sQuery(id+"F9.wireOp",EDGE,"E50.left")])],"isStart":true});
            var Q256;
            Q256=makeQuery(id+"F11.opPattern","COPY",EDGE,{"derivedFrom":makeQuery(id+"F10.opExtrude","SWEPT_EDGE",EDGE,{"disambiguationData":[OSD([sQuery(id+"F9.wireOp",EDGE,"E41.left"),sQuery(id+"F9.wireOp",EDGE,"E45.top")])]}),"instanceName":"1"});
            var Q257;
            Q257=makeQuery(id+"F1.opExtrude","CAP_EDGE",EDGE,{"disambiguationData":[OSD([sQuery(id+"F0.wireOp",EDGE,"E6.trimOffspring")])],"isStart":true});
            var Q258;
            Q258=makeQuery(id+"F4.opExtrude","CAP_EDGE",EDGE,{"disambiguationData":[OSD([sQuery(id+"F3.wireOp",EDGE,"E25.1.0")])],"isStart":true});
            var Q259;
            Q259=makeQuery(id+"F11.opPattern","COPY",EDGE,{"derivedFrom":makeQuery(id+"F10.opExtrude","CAP_EDGE",EDGE,{"disambiguationData":[OSD([sQuery(id+"F9.wireOp",EDGE,"E48.right")])],"isStart":true}),"instanceName":"1"});
            var Q260;
            Q260=makeQuery(id+"F11.opPattern","COPY",EDGE,{"derivedFrom":makeQuery(id+"F10.opExtrude","CAP_EDGE",EDGE,{"disambiguationData":[OSD([sQuery(id+"F9.wireOp",EDGE,"E49.right")])],"isStart":true}),"instanceName":"2"});
            var Q261;
            Q261=makeQuery(id+"F4.opExtrude","CAP_EDGE",EDGE,{"disambiguationData":[OSD([sQuery(id+"F3.wireOp",EDGE,"E20.1.4")])],"isStart":true});
            var Q262;
            Q262=makeQuery(id+"F11.opPattern","COPY",EDGE,{"derivedFrom":makeQuery(id+"F10.opExtrude","CAP_EDGE",EDGE,{"disambiguationData":[OSD([sQuery(id+"F9.wireOp",EDGE,"E48.right")])],"isStart":false}),"instanceName":"2"});
            var Q263;
            Q263=makeQuery(id+"F4.opExtrude","CAP_EDGE",EDGE,{"disambiguationData":[OSD([sQuery(id+"F3.wireOp",EDGE,"E25.2.0")])],"isStart":false});
            var Q264;
            Q264=makeQuery(id+"F10.opExtrude","CAP_EDGE",EDGE,{"disambiguationData":[OSD([sQuery(id+"F9.wireOp",EDGE,"E48.right")])],"isStart":false});
            var Q265;
            Q265=makeQuery(id+"F11.opPattern","COPY",EDGE,{"derivedFrom":makeQuery(id+"F10.opExtrude","CAP_EDGE",EDGE,{"disambiguationData":[OSD([sQuery(id+"F9.wireOp",EDGE,"E41.left")])],"isStart":false}),"instanceName":"1"});
            var Q266;
            Q266=makeQuery(id+"F11.opPattern","COPY",EDGE,{"derivedFrom":makeQuery(id+"F10.opExtrude","CAP_EDGE",EDGE,{"disambiguationData":[OSD([sQuery(id+"F9.wireOp",EDGE,"E41.left")])],"isStart":true}),"instanceName":"2"});
            var Q267;
            Q267=makeQuery(id+"F11.opPattern","COPY",EDGE,{"derivedFrom":makeQuery(id+"F10.opExtrude","CAP_EDGE",EDGE,{"disambiguationData":[OSD([sQuery(id+"F9.wireOp",EDGE,"E41.left")])],"isStart":true}),"instanceName":"1"});
            var Q268;
            Q268=makeQuery(id+"F10.opExtrude","CAP_EDGE",EDGE,{"disambiguationData":[OSD([sQuery(id+"F9.wireOp",EDGE,"E48.right")])],"isStart":true});
            var Q269;
            Q269=makeQuery(id+"F10.opExtrude","CAP_EDGE",EDGE,{"disambiguationData":[OSD([sQuery(id+"F9.wireOp",EDGE,"E41.bottom")])],"isStart":false});
            var Q270;
            Q270=makeQuery(id+"F7.opExtrude","CAP_EDGE",EDGE,{"disambiguationData":[OSD([sQuery(id+"F6.wireOp",EDGE,"E40.2.14")])],"isStart":true});
            var Q271;
            {var subQ0=sQuery(id+"F9.wireOp",EDGE,"E41.left");Q271=qUnion([makeQuery(id+"F11.opPattern","COPY",EDGE,{"derivedFrom":makeQuery(id+"F10.opExtrude","SWEPT_EDGE",EDGE,{"disambiguationData":[OSD([subQ0,sQuery(id+"F9.wireOp",EDGE,"E48.top")])]}),"instanceName":"2"}),makeQuery(id+"F11.opPattern","COPY",EDGE,{"derivedFrom":makeQuery(id+"F10.opExtrude","SWEPT_EDGE",EDGE,{"disambiguationData":[OSD([subQ0,sQuery(id+"F9.wireOp",EDGE,"E45.top")])]}),"instanceName":"2"})]);}
            var Q272;
            Q272=makeQuery(id+"F10.opExtrude","CAP_EDGE",EDGE,{"disambiguationData":[OSD([sQuery(id+"F9.wireOp",EDGE,"E50.left")])],"isStart":false});
            var Q273;
            Q273=makeQuery(id+"F10.opExtrude","CAP_EDGE",EDGE,{"disambiguationData":[OSD([sQuery(id+"F9.wireOp",EDGE,"E45.left")])],"isStart":false});
            var Q274;
            Q274=makeQuery(id+"F7.opExtrude","CAP_EDGE",EDGE,{"disambiguationData":[OSD([sQuery(id+"F6.wireOp",EDGE,"E40.2.14")])],"isStart":false});
            var Q275;
            Q275=makeQuery(id+"F7.opExtrude","CAP_EDGE",EDGE,{"disambiguationData":[OSD([sQuery(id+"F6.wireOp",EDGE,"E40.1.16")])],"isStart":true});
            var Q276;
            Q276=makeQuery(id+"F7.opExtrude","CAP_EDGE",EDGE,{"disambiguationData":[OSD([sQuery(id+"F6.wireOp",EDGE,"E34.filletArc")])],"isStart":true});
            var Q277;
            Q277=makeQuery(id+"F10.opExtrude","CAP_EDGE",EDGE,{"disambiguationData":[OSD([sQuery(id+"F9.wireOp",EDGE,"E45.bottom")])],"isStart":false});
            var Q278;
            Q278=makeQuery(id+"F11.opPattern","COPY",EDGE,{"derivedFrom":makeQuery(id+"F10.opExtrude","CAP_EDGE",EDGE,{"disambiguationData":[OSD([sQuery(id+"F9.wireOp",EDGE,"E48.top")])],"isStart":true}),"instanceName":"2"});
            var Q279;
            Q279=makeQuery(id+"F11.opPattern","COPY",EDGE,{"derivedFrom":makeQuery(id+"F10.opExtrude","CAP_EDGE",EDGE,{"disambiguationData":[OSD([sQuery(id+"F9.wireOp",EDGE,"E48.top")])],"isStart":true}),"instanceName":"1"});
            var Q280;
            Q280=makeQuery(id+"F11.opPattern","COPY",EDGE,{"derivedFrom":makeQuery(id+"F10.opExtrude","SWEPT_EDGE",EDGE,{"disambiguationData":[OSD([sQuery(id+"F9.wireOp",EDGE,"E45.top"),sQuery(id+"F9.wireOp",EDGE,"E45.left")])]}),"instanceName":"2"});
            var Q281;
            Q281=makeQuery(id+"F1.opExtrude","CAP_EDGE",EDGE,{"disambiguationData":[OSD([sQuery(id+"F0.wireOp",EDGE,"E11.2.0")])],"isStart":false});
            var Q282;
            Q282=makeQuery(id+"F7.opExtrude","SWEPT_EDGE",EDGE,{"disambiguationData":[OSD([sQuery(id+"F6.wireOp",EDGE,"E30.1"),sQuery(id+"F6.wireOp",EDGE,"E33.filletArc")])]});
            var Q283;
            Q283=makeQuery(id+"F11.opPattern","COPY",EDGE,{"derivedFrom":makeQuery(id+"F10.opExtrude","CAP_EDGE",EDGE,{"disambiguationData":[OSD([sQuery(id+"F9.wireOp",EDGE,"E41.bottom")])],"isStart":true}),"instanceName":"1"});
            var Q284;
            Q284=makeQuery(id+"F11.opPattern","COPY",EDGE,{"derivedFrom":makeQuery(id+"F10.opExtrude","CAP_EDGE",EDGE,{"disambiguationData":[OSD([sQuery(id+"F9.wireOp",EDGE,"E41.bottom")])],"isStart":true}),"instanceName":"2"});
            var Q285;
            Q285=makeQuery(id+"F10.opExtrude","CAP_EDGE",EDGE,{"disambiguationData":[OSD([sQuery(id+"F9.wireOp",EDGE,"E41.left")])],"isStart":true});
            var Q286;
            Q286=makeQuery(id+"F1.opExtrude","CAP_EDGE",EDGE,{"disambiguationData":[OSD([sQuery(id+"F0.wireOp",EDGE,"E9.2.0")])],"isStart":false});
            var Q287;
            Q287=makeQuery(id+"F7.opExtrude","SWEPT_EDGE",EDGE,{"disambiguationData":[OSD([sQuery(id+"F6.wireOp",EDGE,"E40.1.6"),sQuery(id+"F6.wireOp",EDGE,"E40.1.16")])]});
            var Q288;
            Q288=makeQuery(id+"F7.opExtrude","SWEPT_EDGE",EDGE,{"disambiguationData":[OSD([sQuery(id+"F6.wireOp",EDGE,"E30.0"),sQuery(id+"F6.wireOp",EDGE,"E34.filletArc")])]});
            var Q289;
            Q289=makeQuery(id+"F4.opExtrude","SWEPT_EDGE",EDGE,{"disambiguationData":[OSD([sQuery(id+"F3.wireOp",EDGE,"E18.0.MirrorCS"),sQuery(id+"F3.wireOp",EDGE,"E20.2.0")])]});
            var Q290;
            Q290=makeQuery(id+"F4.opExtrude","SWEPT_EDGE",EDGE,{"disambiguationData":[OSD([sQuery(id+"F3.wireOp",EDGE,"E18.0.MirrorCS"),sQuery(id+"F3.wireOp",EDGE,"E18.1.MirrorCS")])]});
            var Q291;
            Q291=makeQuery(id+"F4.opExtrude","SWEPT_EDGE",EDGE,{"disambiguationData":[OSD([sQuery(id+"F3.wireOp",EDGE,"E14"),sQuery(id+"F3.wireOp",EDGE,"E16")])]});
            var Q292;
            Q292=makeQuery(id+"F4.opExtrude","SWEPT_EDGE",EDGE,{"disambiguationData":[OSD([sQuery(id+"F3.wireOp",EDGE,"E20.2.0"),sQuery(id+"F3.wireOp",EDGE,"E20.2.1")])]});
            var Q293;
            Q293=makeQuery(id+"F4.opExtrude","SWEPT_EDGE",EDGE,{"disambiguationData":[OSD([sQuery(id+"F3.wireOp",EDGE,"E20.1.3"),sQuery(id+"F3.wireOp",EDGE,"E20.1.4")])]});
            var Q294;
            Q294=makeQuery(id+"F11.opPattern","COPY",EDGE,{"derivedFrom":makeQuery(id+"F10.opExtrude","CAP_EDGE",EDGE,{"disambiguationData":[OSD([sQuery(id+"F9.wireOp",EDGE,"E41.left")])],"isStart":true}),"instanceName":"2"});
            var Q295;
            Q295=makeQuery(id+"F11.opPattern","COPY",EDGE,{"derivedFrom":makeQuery(id+"F10.opExtrude","CAP_EDGE",EDGE,{"disambiguationData":[OSD([sQuery(id+"F9.wireOp",EDGE,"E41.left")])],"isStart":true}),"instanceName":"1"});
            var Q296;
            Q296=makeQuery(id+"F7.opExtrude","CAP_EDGE",EDGE,{"disambiguationData":[OSD([sQuery(id+"F6.wireOp",EDGE,"E30.0")])],"isStart":true});
            var Q297;
            Q297=makeQuery(id+"F1.opExtrude","SWEPT_EDGE",EDGE,{"disambiguationData":[OSD([sQuery(id+"F0.wireOp",EDGE,"E1.0"),sQuery(id+"F0.wireOp",EDGE,"E6.trimOffspring")])]});
            var Q298;
            Q298=makeQuery(id+"F1.opExtrude","SWEPT_EDGE",EDGE,{"disambiguationData":[OSD([sQuery(id+"F0.wireOp",EDGE,"E1.2"),sQuery(id+"F0.wireOp",EDGE,"E6.trimOffspring")])]});
            var Q299;
            Q299=makeQuery(id+"F1.opExtrude","CAP_EDGE",EDGE,{"disambiguationData":[OSD([sQuery(id+"F0.wireOp",EDGE,"E0")])],"isStart":true});
            var Q300;
            Q300=makeQuery(id+"F11.opPattern","COPY",EDGE,{"derivedFrom":makeQuery(id+"F10.opExtrude","SWEPT_EDGE",EDGE,{"disambiguationData":[OSD([sQuery(id+"F9.wireOp",EDGE,"E50.bottom"),sQuery(id+"F9.wireOp",EDGE,"E50.left")])]}),"instanceName":"2"});
            var Q301;
            Q301=makeQuery(id+"F11.opPattern","COPY",EDGE,{"derivedFrom":makeQuery(id+"F10.opExtrude","CAP_EDGE",EDGE,{"disambiguationData":[OSD([sQuery(id+"F9.wireOp",EDGE,"E45.top")])],"isStart":false}),"instanceName":"1"});
            var Q302;
            Q302=makeQuery(id+"F1.opExtrude","CAP_EDGE",EDGE,{"disambiguationData":[OSD([sQuery(id+"F0.wireOp",EDGE,"E9.1.0")])],"isStart":true});
            var Q303;
            Q303=makeQuery(id+"F11.opPattern","COPY",EDGE,{"derivedFrom":makeQuery(id+"F10.opExtrude","CAP_EDGE",EDGE,{"disambiguationData":[OSD([sQuery(id+"F9.wireOp",EDGE,"E45.bottom")])],"isStart":true}),"instanceName":"1"});
            var Q304;
            Q304=makeQuery(id+"F11.opPattern","COPY",EDGE,{"derivedFrom":makeQuery(id+"F10.opExtrude","CAP_EDGE",EDGE,{"disambiguationData":[OSD([sQuery(id+"F9.wireOp",EDGE,"E50.bottom")])],"isStart":true}),"instanceName":"2"});
            var Q305;
            Q305=makeQuery(id+"F11.opPattern","COPY",EDGE,{"derivedFrom":makeQuery(id+"F10.opExtrude","SWEPT_EDGE",EDGE,{"disambiguationData":[OSD([sQuery(id+"F9.wireOp",EDGE,"E48.top"),sQuery(id+"F9.wireOp",EDGE,"E48.right")])]}),"instanceName":"2"});
            var Q306;
            Q306=makeQuery(id+"F10.opExtrude","CAP_EDGE",EDGE,{"disambiguationData":[OSD([sQuery(id+"F9.wireOp",EDGE,"E48.top")])],"isStart":false});
            var Q307;
            Q307=makeQuery(id+"F11.opPattern","COPY",EDGE,{"derivedFrom":makeQuery(id+"F10.opExtrude","CAP_EDGE",EDGE,{"disambiguationData":[OSD([sQuery(id+"F9.wireOp",EDGE,"E45.left")])],"isStart":false}),"instanceName":"1"});
            var Q308;
            Q308=makeQuery(id+"F11.opPattern","COPY",EDGE,{"derivedFrom":makeQuery(id+"F10.opExtrude","CAP_EDGE",EDGE,{"disambiguationData":[OSD([sQuery(id+"F9.wireOp",EDGE,"E45.left")])],"isStart":false}),"instanceName":"2"});
            var Q309;
            Q309=makeQuery(id+"F11.opPattern","COPY",EDGE,{"derivedFrom":makeQuery(id+"F10.opExtrude","CAP_EDGE",EDGE,{"disambiguationData":[OSD([sQuery(id+"F9.wireOp",EDGE,"E45.left")])],"isStart":true}),"instanceName":"1"});
            var Q310;
            Q310=makeQuery(id+"F11.opPattern","COPY",EDGE,{"derivedFrom":makeQuery(id+"F10.opExtrude","CAP_EDGE",EDGE,{"disambiguationData":[OSD([sQuery(id+"F9.wireOp",EDGE,"E45.left")])],"isStart":true}),"instanceName":"2"});
            var Q311;
            Q311=makeQuery(id+"F11.opPattern","COPY",EDGE,{"derivedFrom":makeQuery(id+"F10.opExtrude","CAP_EDGE",EDGE,{"disambiguationData":[OSD([sQuery(id+"F9.wireOp",EDGE,"E50.left")])],"isStart":true}),"instanceName":"2"});
            var Q312;
            Q312=makeQuery(id+"F1.opExtrude","CAP_EDGE",EDGE,{"disambiguationData":[OSD([sQuery(id+"F0.wireOp",EDGE,"E8")])],"isStart":false});
            var Q313;
            Q313=makeQuery(id+"F11.opPattern","COPY",EDGE,{"derivedFrom":makeQuery(id+"F10.opExtrude","CAP_EDGE",EDGE,{"disambiguationData":[OSD([sQuery(id+"F9.wireOp",EDGE,"E48.top")])],"isStart":false}),"instanceName":"1"});
            var Q314;
            Q314=makeQuery(id+"F11.opPattern","COPY",EDGE,{"derivedFrom":makeQuery(id+"F10.opExtrude","CAP_EDGE",EDGE,{"disambiguationData":[OSD([sQuery(id+"F9.wireOp",EDGE,"E48.right")])],"isStart":true}),"instanceName":"2"});
            var Q315;
            Q315=makeQuery(id+"F11.opPattern","COPY",EDGE,{"derivedFrom":makeQuery(id+"F10.opExtrude","CAP_EDGE",EDGE,{"disambiguationData":[OSD([sQuery(id+"F9.wireOp",EDGE,"E48.right")])],"isStart":false}),"instanceName":"1"});
            var Q316;
            Q316=makeQuery(id+"F11.opPattern","COPY",EDGE,{"derivedFrom":makeQuery(id+"F10.opExtrude","SWEPT_EDGE",EDGE,{"disambiguationData":[OSD([sQuery(id+"F9.wireOp",EDGE,"E41.left"),sQuery(id+"F9.wireOp",EDGE,"E48.top")])]}),"instanceName":"2"});
            var Q317;
            Q317=makeQuery(id+"F11.opPattern","COPY",EDGE,{"derivedFrom":makeQuery(id+"F10.opExtrude","CAP_EDGE",EDGE,{"disambiguationData":[OSD([sQuery(id+"F9.wireOp",EDGE,"E41.bottom")])],"isStart":false}),"instanceName":"1"});
            var Q318;
            {var subQ0=sQuery(id+"F9.wireOp",EDGE,"E48.right");Q318=qUnion([makeQuery(id+"F11.opPattern","COPY",EDGE,{"derivedFrom":makeQuery(id+"F10.opExtrude","SWEPT_EDGE",EDGE,{"disambiguationData":[OSD([sQuery(id+"F9.wireOp",EDGE,"E41.bottom"),subQ0])]}),"instanceName":"2"}),makeQuery(id+"F11.opPattern","COPY",EDGE,{"derivedFrom":makeQuery(id+"F10.opExtrude","SWEPT_EDGE",EDGE,{"disambiguationData":[OSD([sQuery(id+"F9.wireOp",EDGE,"E48.top"),subQ0])]}),"instanceName":"2"})]);}
            chamfer(context, id + "F12", {"entities" : qUnion([Q0, Q1, Q2, Q3, Q4, Q5, Q6, Q7, Q8, Q9, Q10, Q11, Q12, Q13, Q14, Q15, Q16, Q17, Q18, Q19, Q20, Q21, Q22, Q23, Q24, Q25, Q26, Q27, Q28, Q29, Q30, Q31, Q32, Q33, Q34, Q35, Q36, Q37, Q38, Q39, Q40, Q41, Q42, Q43, Q44, Q45, Q46, Q47, Q48, Q49, Q50, Q51, Q52, Q53, Q54, Q55, Q56, Q57, Q58, Q59, Q60, Q61, Q62, Q63, Q64, Q65, Q66, Q67, Q68, Q69, Q70, Q71, Q72, Q73, Q74, Q75, Q76, Q77, Q78, Q79, Q80, Q81, Q82, Q83, Q84, Q85, Q86, Q87, Q88, Q89, Q90, Q91, Q92, Q93, Q94, Q95, Q96, Q97, Q98, Q99, Q100, Q101, Q102, Q103, Q104, Q105, Q106, Q107, Q108, Q109, Q110, Q111, Q112, Q113, Q114, Q115, Q116, Q117, Q118, Q119, Q120, Q121, Q122, Q123, Q124, Q125, Q126, Q127, Q128, Q129, Q130, Q131, Q132, Q133, Q134, Q135, Q136, Q137, Q138, Q139, Q140, Q141, Q142, Q143, Q144, Q145, Q146, Q147, Q148, Q149, Q150, Q151, Q152, Q153, Q154, Q155, Q156, Q157, Q158, Q159, Q160, Q161, Q162, Q163, Q164, Q165, Q166, Q167, Q168, Q169, Q170, Q171, Q172, Q173, Q174, Q175, Q176, Q177, Q178, Q179, Q180, Q181, Q182, Q183, Q184, Q185, Q186, Q187, Q188, Q189, Q190, Q191, Q192, Q193, Q194, Q195, Q196, Q197, Q198, Q199, Q200, Q201, Q202, Q203, Q204, Q205, Q206, Q207, Q208, Q209, Q210, Q211, Q212, Q213, Q214, Q215, Q216, Q217, Q218, Q219, Q220, Q221, Q222, Q223, Q224, Q225, Q226, Q227, Q228, Q229, Q230, Q231, Q232, Q233, Q234, Q235, Q236, Q237, Q238, Q239, Q240, Q241, Q242, Q243, Q244, Q245, Q246, Q247, Q248, Q249, Q250, Q251, Q252, Q253, Q254, Q255, Q256, Q257, Q258, Q259, Q260, Q261, Q262, Q263, Q264, Q265, Q266, Q267, Q268, Q269, Q270, Q271, Q272, Q273, Q274, Q275, Q276, Q277, Q278, Q279, Q280, Q281, Q282, Q283, Q284, Q285, Q286, Q287, Q288, Q289, Q290, Q291, Q292, Q293, Q294, Q295, Q296, Q297, Q298, Q299, Q300, Q301, Q302, Q303, Q304, Q305, Q306, Q307, Q308, Q309, Q310, Q311, Q312, Q313, Q314, Q315, Q316, Q317, Q318]), "width" : 1 * mm, "tangentPropagation" : true});
        }
        {
            var Q0;
            Q0=makeQuery(id+"F10.opExtrude","SWEPT_FACE",FACE,{"disambiguationData":[OSD([sQuery(id+"F9.wireOp",EDGE,"E49.right")])]});
            var sketch = newSketch(context, id + "F13", { "sketchPlane" : qUnion([Q0])});
            skLineSegment(sketch, "E54", {"start": v(-3.22, 77.63) * mm, "end": v(0, 1) * mm, "construction": true});
            skCircle(sketch, "E55", {"center": v(-2.5, 60.46) * mm, "radius": 2.5 * mm});
            skCircle(sketch, "E56", {"center": v(-0.19, 5.47) * mm, "radius": 2.5 * mm});
            skSolve(sketch);
        }
        {
            var Q0;
            {Q0=qUnion([makeQuery(id+"F13.imprint","IMPRINT",FACE,{"disambiguationData":[TD([[makeQuery(id+"F13.imprint","IMPRINT",EDGE,{"derivedFrom":sQuery(id+"F13.wireOp",EDGE,"E55")}),1.0]])]}),makeQuery(id+"F13.imprint","IMPRINT",FACE,{"disambiguationData":[TD([[makeQuery(id+"F13.imprint","IMPRINT",EDGE,{"derivedFrom":sQuery(id+"F13.wireOp",EDGE,"E56")}),1.0]])]})]);}
            extrude(context, id + "F14", {"entities" : qUnion([Q0]), "depth" : 15 * mm, "symmetric" : true});
        }
        {
            var Q0;
            Q0=makeQuery(id+"F14.opExtrude","SWEPT_BODY",BODY,{"disambiguationData":[OSD([sQuery(id+"F13.wireOp",EDGE,"E56")])]});
            var Q1;
            Q1=makeQuery(id+"F14.opExtrude","SWEPT_BODY",BODY,{"disambiguationData":[OSD([sQuery(id+"F13.wireOp",EDGE,"E55")])]});
            var Q2;
            {var subQ0=sQuery(id+"F3.wireOp",EDGE,"E12.0");Q2=makeQuery(id+"F12.opChamfer","BLEND_EDGE",EDGE,{"blendedFrom":[makeQuery(id+"F4.opExtrude","CAP_EDGE",EDGE,{"disambiguationData":[OSD([subQ0])],"isStart":true}),makeQuery(id+"F4.opExtrude","SWEPT_FACE",FACE,{"disambiguationData":[OSD([subQ0])]})],"blendedInto":[makeQuery(id+"F4.opExtrude","SWEPT_FACE",FACE,{"disambiguationData":[OSD([subQ0])]})]});}
            circularPattern(context, id + "F15", {"entities" : qUnion([Q0, Q1]), "axis" : qUnion([Q2]), "angle" : 120 * degree, "instanceCount" : 3, "computeTransformsWithoutBuiltin" : true});
        }
        {
            var Q0;
            Q0=makeQuery(id+"F15.opPattern","COPY",BODY,{"derivedFrom":makeQuery(id+"F14.opExtrude","SWEPT_BODY",BODY,{"disambiguationData":[OSD([sQuery(id+"F13.wireOp",EDGE,"E55")])]}),"instanceName":"2"});
            var Q1;
            Q1=makeQuery(id+"F15.opPattern","COPY",BODY,{"derivedFrom":makeQuery(id+"F14.opExtrude","SWEPT_BODY",BODY,{"disambiguationData":[OSD([sQuery(id+"F13.wireOp",EDGE,"E56")])]}),"instanceName":"2"});
            var Q2;
            Q2=makeQuery(id+"F14.opExtrude","SWEPT_BODY",BODY,{"disambiguationData":[OSD([sQuery(id+"F13.wireOp",EDGE,"E55")])]});
            var Q3;
            Q3=makeQuery(id+"F14.opExtrude","SWEPT_BODY",BODY,{"disambiguationData":[OSD([sQuery(id+"F13.wireOp",EDGE,"E56")])]});
            var Q4;
            Q4=makeQuery(id+"F15.opPattern","COPY",BODY,{"derivedFrom":makeQuery(id+"F14.opExtrude","SWEPT_BODY",BODY,{"disambiguationData":[OSD([sQuery(id+"F13.wireOp",EDGE,"E55")])]}),"instanceName":"1"});
            var Q5;
            Q5=makeQuery(id+"F15.opPattern","COPY",BODY,{"derivedFrom":makeQuery(id+"F14.opExtrude","SWEPT_BODY",BODY,{"disambiguationData":[OSD([sQuery(id+"F13.wireOp",EDGE,"E56")])]}),"instanceName":"1"});
            var Q6;
            Q6=makeQuery(id+"F11.opPattern","COPY",BODY,{"derivedFrom":makeQuery(id+"F10.opExtrude","SWEPT_BODY",BODY,{"disambiguationData":[OSD([sQuery(id+"F9.wireOp",EDGE,"E41.bottom"),sQuery(id+"F9.wireOp",EDGE,"E41.left"),sQuery(id+"F9.wireOp",EDGE,"E45.top"),sQuery(id+"F9.wireOp",EDGE,"E45.left"),sQuery(id+"F9.wireOp",EDGE,"E46.bottom"),sQuery(id+"F9.wireOp",EDGE,"E46.top"),sQuery(id+"F9.wireOp",EDGE,"E46.right"),sQuery(id+"F9.wireOp",EDGE,"E48.top"),sQuery(id+"F9.wireOp",EDGE,"E48.right"),sQuery(id+"F9.wireOp",EDGE,"E49.right"),sQuery(id+"F9.wireOp",EDGE,"E50.bottom"),sQuery(id+"F9.wireOp",EDGE,"E50.top"),sQuery(id+"F9.wireOp",EDGE,"E50.left"),sQuery(id+"F9.wireOp",EDGE,"E51.trimOffspring"),sQuery(id+"F9.wireOp",EDGE,"E52.trimOffspring"),sQuery(id+"F9.wireOp",EDGE,"E53")])]}),"instanceName":"1"});
            var Q7;
            Q7=makeQuery(id+"F11.opPattern","COPY",BODY,{"derivedFrom":makeQuery(id+"F10.opExtrude","SWEPT_BODY",BODY,{"disambiguationData":[OSD([sQuery(id+"F9.wireOp",EDGE,"E41.bottom"),sQuery(id+"F9.wireOp",EDGE,"E41.left"),sQuery(id+"F9.wireOp",EDGE,"E45.top"),sQuery(id+"F9.wireOp",EDGE,"E45.left"),sQuery(id+"F9.wireOp",EDGE,"E46.bottom"),sQuery(id+"F9.wireOp",EDGE,"E46.top"),sQuery(id+"F9.wireOp",EDGE,"E46.right"),sQuery(id+"F9.wireOp",EDGE,"E48.top"),sQuery(id+"F9.wireOp",EDGE,"E48.right"),sQuery(id+"F9.wireOp",EDGE,"E49.right"),sQuery(id+"F9.wireOp",EDGE,"E50.bottom"),sQuery(id+"F9.wireOp",EDGE,"E50.top"),sQuery(id+"F9.wireOp",EDGE,"E50.left"),sQuery(id+"F9.wireOp",EDGE,"E51.trimOffspring"),sQuery(id+"F9.wireOp",EDGE,"E52.trimOffspring"),sQuery(id+"F9.wireOp",EDGE,"E53")])]}),"instanceName":"2"});
            var Q8;
            Q8=makeQuery(id+"F10.opExtrude","SWEPT_BODY",BODY,{"disambiguationData":[OSD([sQuery(id+"F9.wireOp",EDGE,"E41.bottom"),sQuery(id+"F9.wireOp",EDGE,"E41.left"),sQuery(id+"F9.wireOp",EDGE,"E45.top"),sQuery(id+"F9.wireOp",EDGE,"E45.left"),sQuery(id+"F9.wireOp",EDGE,"E46.bottom"),sQuery(id+"F9.wireOp",EDGE,"E46.top"),sQuery(id+"F9.wireOp",EDGE,"E46.right"),sQuery(id+"F9.wireOp",EDGE,"E48.top"),sQuery(id+"F9.wireOp",EDGE,"E48.right"),sQuery(id+"F9.wireOp",EDGE,"E49.right"),sQuery(id+"F9.wireOp",EDGE,"E50.bottom"),sQuery(id+"F9.wireOp",EDGE,"E50.top"),sQuery(id+"F9.wireOp",EDGE,"E50.left"),sQuery(id+"F9.wireOp",EDGE,"E51.trimOffspring"),sQuery(id+"F9.wireOp",EDGE,"E52.trimOffspring"),sQuery(id+"F9.wireOp",EDGE,"E53")])]});
            booleanBodies(context, id + "F16", {"operationType" : BooleanOperationType.SUBTRACTION, "tools" : qUnion([Q0, Q1, Q2, Q3, Q4, Q5]), "targets" : qUnion([Q6, Q7, Q8])});
        }
    });
